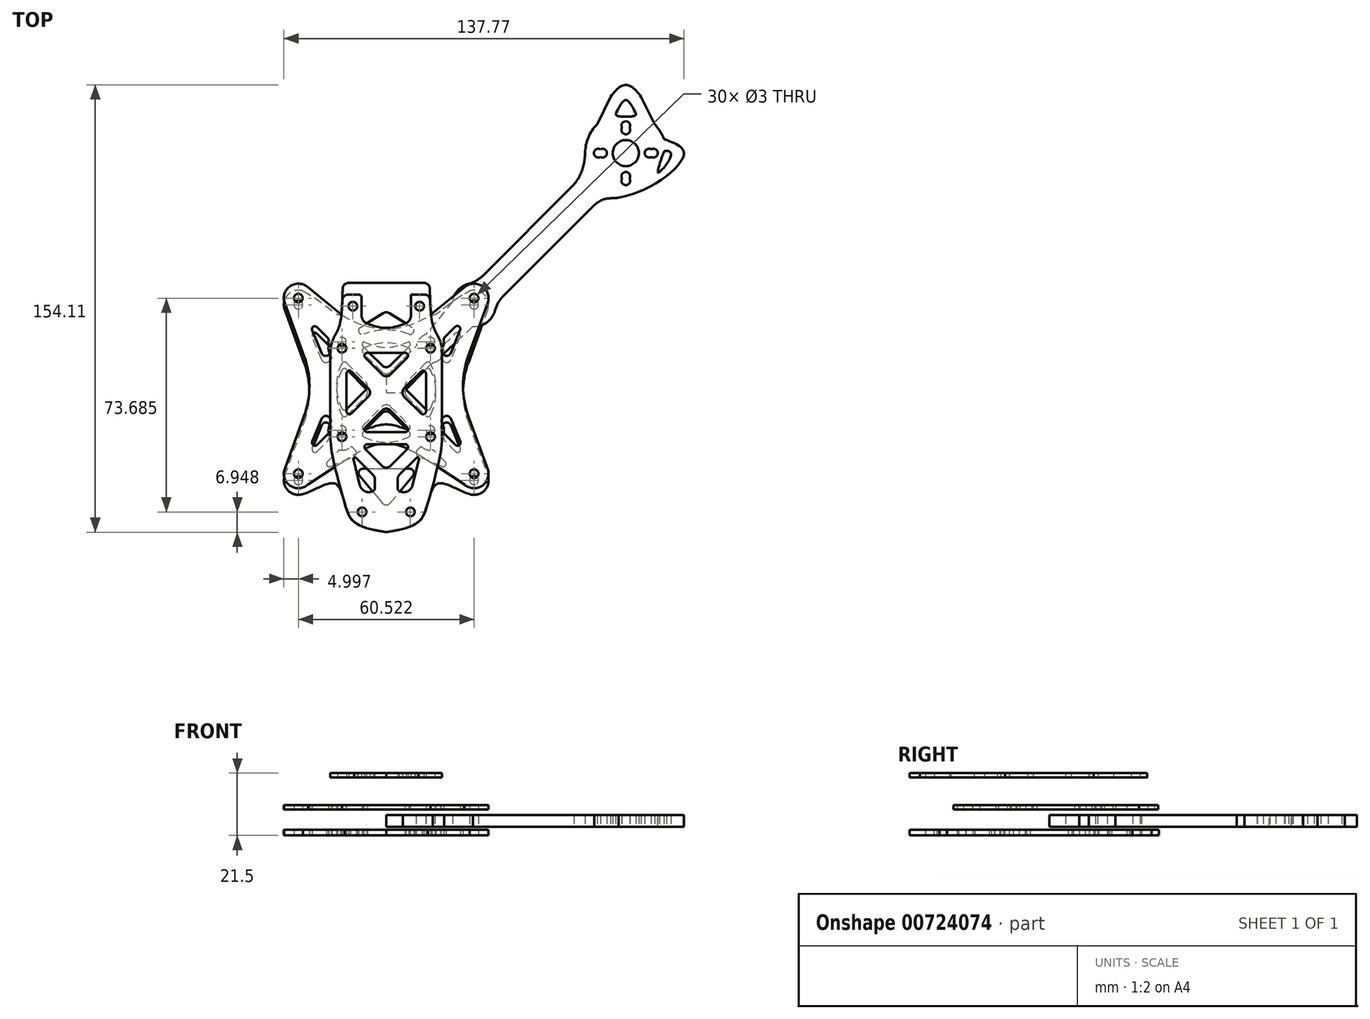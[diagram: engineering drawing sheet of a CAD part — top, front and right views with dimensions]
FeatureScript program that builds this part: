
annotation { "Feature Type Name" : "Feature", "Feature Type Description" : "" }
export const myFeature = defineFeature(function(context is Context, id is Id, definition is map)
    precondition{}
    {
        {
            var Q0;
            Q0=qCreatedBy(makeId("Top.planeOp"),FACE);
            var sketch = newSketch(context, id + "F0", { "sketchPlane" : qUnion([Q0])});
            skLineSegment(sketch, "E0.bottom", {"start": v(-15.25, 15.25) * mm, "end": v(15.25, 15.25) * mm, "construction": true});
            skLineSegment(sketch, "E0.top", {"start": v(-15.25, -15.25) * mm, "end": v(15.25, -15.25) * mm, "construction": true});
            skLineSegment(sketch, "E0.left", {"start": v(-15.25, 15.25) * mm, "end": v(-15.25, -15.25) * mm, "construction": true});
            skLineSegment(sketch, "E0.right", {"start": v(15.25, 15.25) * mm, "end": v(15.25, -15.25) * mm, "construction": true});
            skPoint(sketch, "E0.middle", {"position": v(0, 0) * mm});
            skLineSegment(sketch, "E1.bottom", {"start": v(30.25, 30.25) * mm, "end": v(-30.25, 30.25) * mm, "construction": true});
            skLineSegment(sketch, "E1.top", {"start": v(30.25, -30.25) * mm, "end": v(-30.25, -30.25) * mm, "construction": true});
            skLineSegment(sketch, "E1.left", {"start": v(30.25, 30.25) * mm, "end": v(30.25, -30.25) * mm, "construction": true});
            skLineSegment(sketch, "E1.right", {"start": v(-30.25, 30.25) * mm, "end": v(-30.25, -30.25) * mm, "construction": true});
            skLineSegment(sketch, "E2.bottom", {"start": v(-70.96, 70.96) * mm, "end": v(70.96, 70.96) * mm, "construction": true});
            skLineSegment(sketch, "E2.top", {"start": v(-70.96, -70.96) * mm, "end": v(70.96, -70.96) * mm, "construction": true});
            skLineSegment(sketch, "E2.left", {"start": v(-70.96, 70.96) * mm, "end": v(-70.96, -70.96) * mm, "construction": true});
            skLineSegment(sketch, "E2.right", {"start": v(70.96, 70.96) * mm, "end": v(70.96, -70.96) * mm, "construction": true});
            skCircle(sketch, "E3", {"center": v(70.96, 70.96) * mm, "radius": 8 * mm, "construction": true});
            skCircle(sketch, "E4", {"center": v(70.96, -70.96) * mm, "radius": 8 * mm, "construction": true});
            skCircle(sketch, "E5", {"center": v(-70.96, -70.96) * mm, "radius": 8 * mm, "construction": true});
            skCircle(sketch, "E6", {"center": v(-70.96, 70.96) * mm, "radius": 8 * mm, "construction": true});
            skCircle(sketch, "E7", {"center": v(70.96, 70.96) * mm, "radius": 9.5 * mm, "construction": true});
            skCircle(sketch, "E8", {"center": v(70.96, -70.96) * mm, "radius": 9.5 * mm, "construction": true});
            skCircle(sketch, "E9", {"center": v(-70.96, -70.96) * mm, "radius": 9.5 * mm, "construction": true});
            skCircle(sketch, "E10", {"center": v(-70.96, 70.96) * mm, "radius": 9.5 * mm, "construction": true});
            skCircle(sketch, "E11", {"center": v(70.96, 70.96) * mm, "radius": 14 * mm, "construction": true});
            skCircle(sketch, "E12", {"center": v(-70.96, 70.96) * mm, "radius": 14 * mm, "construction": true});
            skCircle(sketch, "E13", {"center": v(70.96, -70.96) * mm, "radius": 14 * mm, "construction": true});
            skCircle(sketch, "E14", {"center": v(-70.96, -70.96) * mm, "radius": 14 * mm, "construction": true});
            skCircle(sketch, "E15", {"center": v(70.96, 70.96) * mm, "radius": 63.5 * mm, "construction": true});
            skCircle(sketch, "E16", {"center": v(70.96, -70.96) * mm, "radius": 63.5 * mm, "construction": true});
            skCircle(sketch, "E17", {"center": v(-70.96, -70.96) * mm, "radius": 63.5 * mm, "construction": true});
            skCircle(sketch, "E18", {"center": v(-70.96, 70.96) * mm, "radius": 63.5 * mm, "construction": true});
            skLineSegment(sketch, "E19", {"start": v(0, 30.25) * mm, "end": v(0, 37.76) * mm, "construction": true});
            skLineSegment(sketch, "E20", {"start": v(0, 37.76) * mm, "end": v(-15, 37.76) * mm, "construction": true});
            skLineSegment(sketch, "E21", {"start": v(0, 37.76) * mm, "end": v(15, 37.76) * mm, "construction": true});
            skLineSegment(sketch, "E22", {"start": v(0, -30.25) * mm, "end": v(0, -37.76) * mm, "construction": true});
            skLineSegment(sketch, "E23.bottom", {"start": v(-26.17, 26.25) * mm, "end": v(26.21, 26.25) * mm, "construction": true});
            skLineSegment(sketch, "E23.top", {"start": v(-26.21, -26.25) * mm, "end": v(26.17, -26.25) * mm, "construction": true});
            skLineSegment(sketch, "E23.left", {"start": v(-26.17, 26.25) * mm, "end": v(-26.17, -26.13) * mm, "construction": true});
            skLineSegment(sketch, "E23.right", {"start": v(26.21, 26.25) * mm, "end": v(26.21, -26.2) * mm, "construction": true});
            skCircle(sketch, "E24", {"center": v(30.25, 30.25) * mm, "radius": 5 * mm, "construction": true});
            skCircle(sketch, "E25", {"center": v(-30.25, 30.25) * mm, "radius": 5 * mm, "construction": true});
            skCircle(sketch, "E26", {"center": v(30.25, -30.25) * mm, "radius": 5 * mm, "construction": true});
            skCircle(sketch, "E27", {"center": v(-30.25, -30.25) * mm, "radius": 5 * mm, "construction": true});
            skLineSegment(sketch, "E28.bottom", {"start": v(24.5, 24.5) * mm, "end": v(-24.5, 24.5) * mm, "construction": true});
            skLineSegment(sketch, "E28.top", {"start": v(24.5, -24.5) * mm, "end": v(-24.5, -24.5) * mm, "construction": true});
            skLineSegment(sketch, "E28.left", {"start": v(24.5, 24.5) * mm, "end": v(24.5, -24.5) * mm, "construction": true});
            skLineSegment(sketch, "E28.right", {"start": v(-24.5, 24.5) * mm, "end": v(-24.5, -24.5) * mm, "construction": true});
            skLineSegment(sketch, "E29", {"start": v(-26.17, 26.25) * mm, "end": v(-30.25, 30.25) * mm, "construction": true});
            skLineSegment(sketch, "E30", {"start": v(-26.68, 26.75) * mm, "end": v(-33.82, 33.75) * mm, "construction": true});
            skLineSegment(sketch, "E31", {"start": v(-31.8, 31.77) * mm, "end": v(-28.66, 34.99) * mm, "construction": true});
            skLineSegment(sketch, "E32", {"start": v(-31.8, 31.77) * mm, "end": v(-34.96, 28.56) * mm, "construction": true});
            skArc(sketch, "E33", {"start": v(-28.66, 34.99) * mm, "mid": v(-33.82, 33.75) * mm, "end": v(-34.96, 28.56) * mm});
            skLineSegment(sketch, "E34", {"start": v(26.21, 26.25) * mm, "end": v(30.25, 30.25) * mm, "construction": true});
            skLineSegment(sketch, "E35", {"start": v(26.7, 26.73) * mm, "end": v(33.8, 33.77) * mm, "construction": true});
            skLineSegment(sketch, "E36", {"start": v(31.8, 31.78) * mm, "end": v(34.96, 28.58) * mm, "construction": true});
            skLineSegment(sketch, "E37", {"start": v(31.8, 31.78) * mm, "end": v(28.63, 34.98) * mm, "construction": true});
            skArc(sketch, "E38", {"start": v(34.96, 28.58) * mm, "mid": v(33.8, 33.77) * mm, "end": v(28.63, 34.98) * mm});
            skLineSegment(sketch, "E39", {"start": v(26.17, -26.25) * mm, "end": v(30.25, -30.25) * mm, "construction": true});
            skLineSegment(sketch, "E40", {"start": v(26.68, -26.75) * mm, "end": v(33.82, -33.75) * mm, "construction": true});
            skLineSegment(sketch, "E41", {"start": v(31.8, -31.77) * mm, "end": v(34.96, -28.56) * mm, "construction": true});
            skLineSegment(sketch, "E42", {"start": v(31.8, -31.77) * mm, "end": v(28.66, -34.99) * mm, "construction": true});
            skArc(sketch, "E43", {"start": v(28.66, -34.99) * mm, "mid": v(33.82, -33.75) * mm, "end": v(34.96, -28.56) * mm});
            skLineSegment(sketch, "E44", {"start": v(-26.21, -26.25) * mm, "end": v(-30.25, -30.25) * mm, "construction": true});
            skLineSegment(sketch, "E45", {"start": v(-26.7, -26.73) * mm, "end": v(-33.8, -33.77) * mm, "construction": true});
            skLineSegment(sketch, "E46", {"start": v(-31.8, -31.78) * mm, "end": v(-28.63, -34.98) * mm, "construction": true});
            skLineSegment(sketch, "E47", {"start": v(-31.8, -31.78) * mm, "end": v(-34.96, -28.58) * mm, "construction": true});
            skArc(sketch, "E48", {"start": v(-34.96, -28.58) * mm, "mid": v(-33.8, -33.77) * mm, "end": v(-28.63, -34.98) * mm});
            skLineSegment(sketch, "E49", {"start": v(-34.96, -28.58) * mm, "end": v(-28.28, -10.31) * mm});
            skLineSegment(sketch, "E50", {"start": v(-28.28, 10.31) * mm, "end": v(-34.96, 28.56) * mm});
            skLineSegment(sketch, "E51", {"start": v(34.96, 28.58) * mm, "end": v(28.28, 10.31) * mm});
            skLineSegment(sketch, "E52", {"start": v(28.28, -10.31) * mm, "end": v(34.96, -28.56) * mm});
            skPoint(sketch, "E53.visualSharp", {"position": v(24.5, 0) * mm});
            skArc(sketch, "E53.filletArc", {"start": v(28.28, 10.31) * mm, "mid": v(26.45, 0) * mm, "end": v(28.28, -10.31) * mm});
            skPoint(sketch, "E54.visualSharp", {"position": v(-24.5, 0) * mm});
            skArc(sketch, "E54.filletArc", {"start": v(-28.28, -10.31) * mm, "mid": v(-26.45, 0) * mm, "end": v(-28.28, 10.31) * mm});
            skFitSpline(sketch, "E55", {"points": [v(-28.66, 34.99) * mm, v(-15, 37.76) * mm], "startDerivative": vector(40.9, -21.49) * mm, "endDerivative": vector(0.75, 54.16) * mm});
            skFitSpline(sketch, "E56", {"points": [v(15, 37.76) * mm, v(28.63, 34.98) * mm], "startDerivative": vector(0.75, -54.16) * mm, "endDerivative": vector(40.9, 21.46) * mm});
            skLineSegment(sketch, "E57", {"start": v(-15.25, 19.7) * mm, "end": v(15.25, 19.7) * mm, "construction": true});
            skPoint(sketch, "E58.endSnap0", {"position": v(0, -15.25) * mm});
            skLineSegment(sketch, "E59", {"start": v(-15.25, -19.7) * mm, "end": v(15.25, -19.7) * mm, "construction": true});
            skLineSegment(sketch, "E60", {"start": v(-14.33, -37.76) * mm, "end": v(14.33, -37.76) * mm, "construction": true});
            skLineSegment(sketch, "E61", {"start": v(-13.03, 37.76) * mm, "end": v(13.03, 37.76) * mm});
            skCircle(sketch, "E62", {"center": v(-30.25, 30.25) * mm, "radius": 1.5 * mm});
            skCircle(sketch, "E63", {"center": v(30.25, 30.25) * mm, "radius": 1.5 * mm});
            skCircle(sketch, "E64", {"center": v(15.25, 15.25) * mm, "radius": 1.5 * mm});
            skCircle(sketch, "E65", {"center": v(-15.25, 15.25) * mm, "radius": 1.5 * mm});
            skCircle(sketch, "E66", {"center": v(-15.25, -15.25) * mm, "radius": 1.5 * mm});
            skCircle(sketch, "E67", {"center": v(15.25, -15.25) * mm, "radius": 1.5 * mm});
            skCircle(sketch, "E68", {"center": v(30.25, -30.25) * mm, "radius": 1.5 * mm});
            skCircle(sketch, "E69", {"center": v(-30.25, -30.25) * mm, "radius": 1.5 * mm});
            skLineSegment(sketch, "E70", {"start": v(15, 37.76) * mm, "end": v(11.5, 37.76) * mm, "construction": true});
            skLineSegment(sketch, "E71", {"start": v(-15, 37.76) * mm, "end": v(-11.5, 37.76) * mm, "construction": true});
            skLineSegment(sketch, "E72", {"start": v(11.5, 37.76) * mm, "end": v(11.5, 29.76) * mm, "construction": true});
            skLineSegment(sketch, "E73", {"start": v(-11.5, 37.76) * mm, "end": v(-11.5, 29.76) * mm, "construction": true});
            skCircle(sketch, "E74", {"center": v(-11.5, 29.76) * mm, "radius": 1.5 * mm});
            skCircle(sketch, "E75", {"center": v(11.5, 29.76) * mm, "radius": 1.5 * mm});
            skLineSegment(sketch, "E76", {"start": v(0, 37.76) * mm, "end": v(0, 15.25) * mm, "construction": true});
            skLineSegment(sketch, "E77", {"start": v(0, -44.58) * mm, "end": v(-11, -44.58) * mm, "construction": true});
            skLineSegment(sketch, "E78", {"start": v(0, -44.58) * mm, "end": v(11, -44.58) * mm, "construction": true});
            skPoint(sketch, "E79.visualSharp", {"position": v(-14.33, -37.76) * mm});
            skPoint(sketch, "E80.visualSharp", {"position": v(14.33, -37.76) * mm});
            skCircle(sketch, "E81", {"center": v(0, 0) * mm, "radius": 17.11 * mm, "construction": true});
            skLineSegment(sketch, "E82", {"start": v(0, 0) * mm, "end": v(14.1, 14.1) * mm, "construction": true});
            skLineSegment(sketch, "E83", {"start": v(0, 0) * mm, "end": v(-15.25, 15.25) * mm, "construction": true});
            skLineSegment(sketch, "E84", {"start": v(0, 0) * mm, "end": v(-15.32, -15.32) * mm, "construction": true});
            skLineSegment(sketch, "E85", {"start": v(0, 0) * mm, "end": v(15.25, -15.25) * mm, "construction": true});
            skLineSegment(sketch, "E86", {"start": v(-10.7, 10.7) * mm, "end": v(-7.86, 13.52) * mm, "construction": true});
            skLineSegment(sketch, "E87", {"start": v(-10.7, 10.7) * mm, "end": v(-13.52, 7.86) * mm, "construction": true});
            skLineSegment(sketch, "E88", {"start": v(9.03, 9.03) * mm, "end": v(11.86, 6.2) * mm, "construction": true});
            skLineSegment(sketch, "E89", {"start": v(9.03, 9.03) * mm, "end": v(6.2, 11.86) * mm, "construction": true});
            skLineSegment(sketch, "E90", {"start": v(9.8, -9.8) * mm, "end": v(12.64, -6.98) * mm, "construction": true});
            skLineSegment(sketch, "E91", {"start": v(9.8, -9.8) * mm, "end": v(6.98, -12.64) * mm, "construction": true});
            skLineSegment(sketch, "E92", {"start": v(-9.52, -9.52) * mm, "end": v(-6.7, -12.35) * mm, "construction": true});
            skLineSegment(sketch, "E93", {"start": v(-9.52, -9.52) * mm, "end": v(-12.35, -6.7) * mm, "construction": true});
            skLineSegment(sketch, "E94.bottom", {"start": v(6.35, 6.35) * mm, "end": v(-6.35, 6.35) * mm, "construction": true});
            skLineSegment(sketch, "E94.top", {"start": v(6.35, -6.35) * mm, "end": v(-6.35, -6.35) * mm, "construction": true});
            skLineSegment(sketch, "E94.left", {"start": v(6.35, 6.35) * mm, "end": v(6.35, -6.35) * mm, "construction": true});
            skLineSegment(sketch, "E94.right", {"start": v(-6.35, 6.35) * mm, "end": v(-6.35, -6.35) * mm, "construction": true});
            skLineSegment(sketch, "E95", {"start": v(6.2, 11.86) * mm, "end": v(8.94, 14.6) * mm, "construction": true});
            skLineSegment(sketch, "E96", {"start": v(11.86, 6.2) * mm, "end": v(14.6, 8.94) * mm, "construction": true});
            skLineSegment(sketch, "E97", {"start": v(8, 13.66) * mm, "end": v(1.41, 7.07) * mm});
            skLineSegment(sketch, "E98", {"start": v(-1.41, 7.07) * mm, "end": v(-8, 13.66) * mm});
            skLineSegment(sketch, "E99", {"start": v(-13.52, 7.86) * mm, "end": v(-14.6, 8.94) * mm, "construction": true});
            skLineSegment(sketch, "E100", {"start": v(-6.7, -12.35) * mm, "end": v(-8.94, -14.6) * mm, "construction": true});
            skLineSegment(sketch, "E101", {"start": v(-8, -13.66) * mm, "end": v(-1.41, -7.07) * mm});
            skLineSegment(sketch, "E102", {"start": v(1.41, -7.07) * mm, "end": v(8, -13.66) * mm});
            skLineSegment(sketch, "E103", {"start": v(13.66, 8) * mm, "end": v(7.07, 1.41) * mm});
            skLineSegment(sketch, "E104", {"start": v(7.07, -1.41) * mm, "end": v(13.66, -8) * mm});
            skPoint(sketch, "E105", {"position": v(-7.77, 15.25) * mm});
            skPoint(sketch, "E106", {"position": v(7.77, 15.25) * mm});
            skPoint(sketch, "E107", {"position": v(15.25, 7.77) * mm});
            skPoint(sketch, "E108", {"position": v(15.25, -7.77) * mm});
            skPoint(sketch, "E109", {"position": v(7.77, -15.25) * mm});
            skPoint(sketch, "E110", {"position": v(-7.77, -15.25) * mm});
            skPoint(sketch, "E111", {"position": v(-15.25, -7.77) * mm});
            skPoint(sketch, "E112", {"position": v(-15.25, 7.77) * mm});
            skLineSegment(sketch, "E113", {"start": v(-7.79, 15.24) * mm, "end": v(-7.77, 15.25) * mm});
            skLineSegment(sketch, "E114", {"start": v(7.79, 15.24) * mm, "end": v(7.77, 15.25) * mm});
            skLineSegment(sketch, "E115", {"start": v(15.24, 7.79) * mm, "end": v(15.25, 7.77) * mm});
            skLineSegment(sketch, "E116", {"start": v(15.24, -7.79) * mm, "end": v(15.25, -7.77) * mm});
            skLineSegment(sketch, "E117", {"start": v(7.79, -15.24) * mm, "end": v(7.77, -15.25) * mm});
            skLineSegment(sketch, "E118", {"start": v(-7.77, -15.25) * mm, "end": v(-7.79, -15.24) * mm});
            skLineSegment(sketch, "E119", {"start": v(-15.24, -7.79) * mm, "end": v(-15.25, -7.77) * mm});
            skLineSegment(sketch, "E120", {"start": v(-15.24, 7.79) * mm, "end": v(-15.25, 7.77) * mm});
            skPoint(sketch, "E121", {"position": v(0, 17.11) * mm});
            skPoint(sketch, "E122", {"position": v(17.11, 0) * mm});
            skPoint(sketch, "E123", {"position": v(-17.11, 0) * mm});
            skPoint(sketch, "E124", {"position": v(0, -17.11) * mm});
            skArc(sketch, "E125", {"start": v(7.77, 15.25) * mm, "mid": v(0, 17.11) * mm, "end": v(-7.77, 15.25) * mm});
            skArc(sketch, "E126", {"start": v(15.25, -7.77) * mm, "mid": v(17.11, 0) * mm, "end": v(15.25, 7.77) * mm});
            skArc(sketch, "E127", {"start": v(-7.77, -15.25) * mm, "mid": v(0, -17.11) * mm, "end": v(7.77, -15.25) * mm});
            skArc(sketch, "E128", {"start": v(-15.25, 7.77) * mm, "mid": v(-17.11, 0) * mm, "end": v(-15.25, -7.77) * mm});
            skPoint(sketch, "E129.visualSharp", {"position": v(-5.66, 0) * mm});
            skPoint(sketch, "E130.visualSharp", {"position": v(-14.6, 8.94) * mm});
            skArc(sketch, "E130.filletArc", {"start": v(-13.66, 8) * mm, "mid": v(-14.5, 8.29) * mm, "end": v(-15.24, 7.79) * mm});
            skPoint(sketch, "E131.visualSharp", {"position": v(-14.6, -8.94) * mm});
            skArc(sketch, "E131.filletArc", {"start": v(-15.24, -7.79) * mm, "mid": v(-14.5, -8.29) * mm, "end": v(-13.66, -8) * mm});
            skPoint(sketch, "E132.visualSharp", {"position": v(-8.94, 14.6) * mm});
            skArc(sketch, "E132.filletArc", {"start": v(-7.79, 15.24) * mm, "mid": v(-8.29, 14.5) * mm, "end": v(-8, 13.66) * mm});
            skPoint(sketch, "E133.visualSharp", {"position": v(8.94, 14.6) * mm});
            skArc(sketch, "E133.filletArc", {"start": v(8, 13.66) * mm, "mid": v(8.29, 14.5) * mm, "end": v(7.79, 15.24) * mm});
            skPoint(sketch, "E134.visualSharp", {"position": v(14.6, -8.94) * mm});
            skArc(sketch, "E134.filletArc", {"start": v(13.66, -8) * mm, "mid": v(14.5, -8.29) * mm, "end": v(15.24, -7.79) * mm});
            skPoint(sketch, "E135.visualSharp", {"position": v(14.6, 8.94) * mm});
            skArc(sketch, "E135.filletArc", {"start": v(15.24, 7.79) * mm, "mid": v(14.5, 8.29) * mm, "end": v(13.66, 8) * mm});
            skPoint(sketch, "E136.visualSharp", {"position": v(8.94, -14.6) * mm});
            skArc(sketch, "E136.filletArc", {"start": v(7.79, -15.24) * mm, "mid": v(8.29, -14.5) * mm, "end": v(8, -13.66) * mm});
            skPoint(sketch, "E137.visualSharp", {"position": v(-8.94, -14.6) * mm});
            skArc(sketch, "E137.filletArc", {"start": v(-8, -13.66) * mm, "mid": v(-8.29, -14.5) * mm, "end": v(-7.79, -15.24) * mm});
            skLineSegment(sketch, "E138", {"start": v(-13.66, 8) * mm, "end": v(-7.07, 1.41) * mm});
            skLineSegment(sketch, "E139", {"start": v(-13.66, -8) * mm, "end": v(-7.07, -1.41) * mm});
            skArc(sketch, "E140.filletArc", {"start": v(-7.07, -1.41) * mm, "mid": v(-6.49, 0) * mm, "end": v(-7.07, 1.41) * mm});
            skPoint(sketch, "E141.visualSharp", {"position": v(0, -5.66) * mm});
            skArc(sketch, "E141.filletArc", {"start": v(1.41, -7.07) * mm, "mid": v(0, -6.49) * mm, "end": v(-1.41, -7.07) * mm});
            skPoint(sketch, "E142.visualSharp", {"position": v(5.66, 0) * mm});
            skArc(sketch, "E142.filletArc", {"start": v(7.07, 1.41) * mm, "mid": v(6.49, 0) * mm, "end": v(7.07, -1.41) * mm});
            skPoint(sketch, "E143.visualSharp", {"position": v(0, 5.66) * mm});
            skArc(sketch, "E143.filletArc", {"start": v(-1.41, 7.07) * mm, "mid": v(0, 6.49) * mm, "end": v(1.41, 7.07) * mm});
            skLineSegment(sketch, "E144", {"start": v(-12.9, 12.9) * mm, "end": v(-11.14, 14.67) * mm, "construction": true});
            skLineSegment(sketch, "E145", {"start": v(-12.9, 12.9) * mm, "end": v(-14.67, 11.14) * mm, "construction": true});
            skLineSegment(sketch, "E146", {"start": v(-14.67, 11.14) * mm, "end": v(-27.4, 23.87) * mm, "construction": true});
            skPoint(sketch, "E147", {"position": v(-17.57, 14.03) * mm});
            skCircle(sketch, "E148", {"center": v(-15.25, 15.25) * mm, "radius": 4.62 * mm, "construction": true});
            skLineSegment(sketch, "E149", {"start": v(-27.4, 23.87) * mm, "end": v(-21.1, 8.64) * mm, "construction": true});
            skLineSegment(sketch, "E150", {"start": v(-15.25, 15.25) * mm, "end": v(-21.32, 9.18) * mm, "construction": true});
            skLineSegment(sketch, "E151", {"start": v(-18.86, 11.64) * mm, "end": v(-19.74, 10.76) * mm});
            skLineSegment(sketch, "E152", {"start": v(-22.18, 11.25) * mm, "end": v(-25.48, 19.23) * mm});
            skLineSegment(sketch, "E153", {"start": v(-23.85, 20.32) * mm, "end": v(-20.04, 16.5) * mm});
            skLineSegment(sketch, "E154", {"start": v(-19.83, 15.85) * mm, "end": v(-19.85, 15.74) * mm});
            skLineSegment(sketch, "E155", {"start": v(-18.84, 12.33) * mm, "end": v(-18.85, 12.35) * mm});
            skPoint(sketch, "E156", {"position": v(-19.67, 13.9) * mm});
            skArc(sketch, "E157", {"start": v(-19.85, 15.74) * mm, "mid": v(-19.69, 13.95) * mm, "end": v(-18.85, 12.35) * mm});
            skPoint(sketch, "E158.visualSharp", {"position": v(-27.4, 23.87) * mm});
            skArc(sketch, "E158.filletArc", {"start": v(-23.85, 20.32) * mm, "mid": v(-25.11, 20.44) * mm, "end": v(-25.48, 19.23) * mm});
            skPoint(sketch, "E159.visualSharp", {"position": v(-21.32, 9.18) * mm});
            skArc(sketch, "E159.filletArc", {"start": v(-22.18, 11.25) * mm, "mid": v(-21.1, 10.35) * mm, "end": v(-19.74, 10.76) * mm});
            skPoint(sketch, "E160.visualSharp", {"position": v(-18.52, 11.98) * mm});
            skArc(sketch, "E160.filletArc", {"start": v(-18.86, 11.64) * mm, "mid": v(-18.7, 11.98) * mm, "end": v(-18.84, 12.33) * mm});
            skPoint(sketch, "E161.visualSharp", {"position": v(-19.77, 16.23) * mm});
            skArc(sketch, "E161.filletArc", {"start": v(-19.83, 15.85) * mm, "mid": v(-19.86, 16.2) * mm, "end": v(-20.04, 16.5) * mm});
            skCircle(sketch, "E162", {"center": v(15.23, 15.26) * mm, "radius": 4.62 * mm, "construction": true});
            skLineSegment(sketch, "E163", {"start": v(15.23, 15.26) * mm, "end": v(12.9, 12.9) * mm, "construction": true});
            skLineSegment(sketch, "E164", {"start": v(12.9, 12.9) * mm, "end": v(14.68, 11.15) * mm, "construction": true});
            skLineSegment(sketch, "E165", {"start": v(12.9, 12.9) * mm, "end": v(11.12, 14.66) * mm, "construction": true});
            skLineSegment(sketch, "E166", {"start": v(11.12, 14.66) * mm, "end": v(23.85, 27.39) * mm, "construction": true});
            skLineSegment(sketch, "E167", {"start": v(14.68, 11.15) * mm, "end": v(27.32, 23.97) * mm, "construction": true});
            skLineSegment(sketch, "E168", {"start": v(15.25, 15.25) * mm, "end": v(21.37, 9.22) * mm, "construction": true});
            skLineSegment(sketch, "E169", {"start": v(21.37, 9.22) * mm, "end": v(27.32, 23.97) * mm, "construction": true});
            skLineSegment(sketch, "E170", {"start": v(19.8, 15.9) * mm, "end": v(19.82, 15.79) * mm});
            skLineSegment(sketch, "E171", {"start": v(18.84, 12.37) * mm, "end": v(18.86, 12.4) * mm});
            skLineSegment(sketch, "E172", {"start": v(20.01, 16.55) * mm, "end": v(23.8, 20.4) * mm});
            skLineSegment(sketch, "E173", {"start": v(25.45, 19.33) * mm, "end": v(22.2, 11.3) * mm});
            skLineSegment(sketch, "E174", {"start": v(19.77, 10.8) * mm, "end": v(18.86, 11.69) * mm});
            skPoint(sketch, "E175", {"position": v(19.65, 13.92) * mm});
            skArc(sketch, "E176", {"start": v(18.86, 12.4) * mm, "mid": v(19.68, 14) * mm, "end": v(19.82, 15.79) * mm});
            skPoint(sketch, "E177.visualSharp", {"position": v(18.53, 12.02) * mm});
            skArc(sketch, "E177.filletArc", {"start": v(18.84, 12.37) * mm, "mid": v(18.72, 12.03) * mm, "end": v(18.86, 11.69) * mm});
            skPoint(sketch, "E178.visualSharp", {"position": v(19.74, 16.28) * mm});
            skArc(sketch, "E178.filletArc", {"start": v(20.01, 16.55) * mm, "mid": v(19.83, 16.25) * mm, "end": v(19.8, 15.9) * mm});
            skPoint(sketch, "E179.visualSharp", {"position": v(27.32, 23.97) * mm});
            skArc(sketch, "E179.filletArc", {"start": v(25.45, 19.33) * mm, "mid": v(25.07, 20.54) * mm, "end": v(23.8, 20.4) * mm});
            skPoint(sketch, "E180.visualSharp", {"position": v(21.37, 9.22) * mm});
            skArc(sketch, "E180.filletArc", {"start": v(19.77, 10.8) * mm, "mid": v(21.12, 10.4) * mm, "end": v(22.2, 11.3) * mm});
            skCircle(sketch, "E181", {"center": v(-15.25, -15.25) * mm, "radius": 4.62 * mm, "construction": true});
            skCircle(sketch, "E182", {"center": v(15.25, -15.25) * mm, "radius": 4.62 * mm, "construction": true});
            skLineSegment(sketch, "E183", {"start": v(-15.25, -15.25) * mm, "end": v(-12.9, -12.9) * mm, "construction": true});
            skLineSegment(sketch, "E184", {"start": v(-12.9, -12.9) * mm, "end": v(-11.14, -14.67) * mm, "construction": true});
            skLineSegment(sketch, "E185", {"start": v(-12.9, -12.9) * mm, "end": v(-14.67, -11.14) * mm, "construction": true});
            skLineSegment(sketch, "E186", {"start": v(-11.14, -14.67) * mm, "end": v(-23.87, -27.4) * mm, "construction": true});
            skLineSegment(sketch, "E187", {"start": v(-14.67, -11.14) * mm, "end": v(-27.4, -23.87) * mm, "construction": true});
            skLineSegment(sketch, "E188", {"start": v(-15.25, -15.25) * mm, "end": v(-9.18, -21.32) * mm, "construction": true});
            skLineSegment(sketch, "E189", {"start": v(-15.25, -15.25) * mm, "end": v(-21.32, -9.18) * mm, "construction": true});
            skLineSegment(sketch, "E190", {"start": v(-25.48, -19.23) * mm, "end": v(-22.18, -11.25) * mm});
            skLineSegment(sketch, "E191", {"start": v(-19.74, -10.76) * mm, "end": v(-18.86, -11.64) * mm});
            skLineSegment(sketch, "E192", {"start": v(-23.85, -20.32) * mm, "end": v(-20.04, -16.5) * mm});
            skLineSegment(sketch, "E193", {"start": v(-18.84, -12.33) * mm, "end": v(-18.85, -12.35) * mm});
            skLineSegment(sketch, "E194", {"start": v(-19.83, -15.85) * mm, "end": v(-19.85, -15.74) * mm});
            skPoint(sketch, "E195", {"position": v(-19.69, -13.94) * mm});
            skArc(sketch, "E196", {"start": v(-18.85, -12.35) * mm, "mid": v(-19.69, -13.95) * mm, "end": v(-19.85, -15.74) * mm});
            skPoint(sketch, "E197.visualSharp", {"position": v(-18.52, -11.98) * mm});
            skArc(sketch, "E197.filletArc", {"start": v(-18.84, -12.33) * mm, "mid": v(-18.7, -11.98) * mm, "end": v(-18.86, -11.64) * mm});
            skPoint(sketch, "E198.visualSharp", {"position": v(-19.77, -16.23) * mm});
            skArc(sketch, "E198.filletArc", {"start": v(-20.04, -16.5) * mm, "mid": v(-19.86, -16.2) * mm, "end": v(-19.83, -15.85) * mm});
            skPoint(sketch, "E199.visualSharp", {"position": v(-27.4, -23.87) * mm});
            skArc(sketch, "E199.filletArc", {"start": v(-25.48, -19.23) * mm, "mid": v(-25.11, -20.44) * mm, "end": v(-23.85, -20.32) * mm});
            skPoint(sketch, "E200.visualSharp", {"position": v(-21.32, -9.18) * mm});
            skArc(sketch, "E200.filletArc", {"start": v(-19.74, -10.76) * mm, "mid": v(-21.1, -10.35) * mm, "end": v(-22.18, -11.25) * mm});
            skLineSegment(sketch, "E201", {"start": v(15.25, -15.25) * mm, "end": v(12.9, -12.9) * mm, "construction": true});
            skLineSegment(sketch, "E202", {"start": v(12.9, -12.9) * mm, "end": v(14.67, -11.14) * mm, "construction": true});
            skLineSegment(sketch, "E203", {"start": v(12.9, -12.9) * mm, "end": v(11.14, -14.67) * mm, "construction": true});
            skLineSegment(sketch, "E204", {"start": v(14.67, -11.14) * mm, "end": v(27.4, -23.87) * mm, "construction": true});
            skLineSegment(sketch, "E205", {"start": v(15.25, -15.25) * mm, "end": v(21.32, -9.18) * mm, "construction": true});
            skLineSegment(sketch, "E206", {"start": v(22.18, -11.25) * mm, "end": v(25.48, -19.23) * mm});
            skLineSegment(sketch, "E207", {"start": v(23.85, -20.32) * mm, "end": v(20.04, -16.5) * mm});
            skLineSegment(sketch, "E208", {"start": v(19.74, -10.76) * mm, "end": v(18.86, -11.64) * mm});
            skLineSegment(sketch, "E209", {"start": v(18.84, -12.33) * mm, "end": v(18.85, -12.35) * mm});
            skLineSegment(sketch, "E210", {"start": v(19.83, -15.85) * mm, "end": v(19.85, -15.74) * mm});
            skPoint(sketch, "E211", {"position": v(19.64, -13.8) * mm});
            skArc(sketch, "E212", {"start": v(19.85, -15.74) * mm, "mid": v(19.69, -13.95) * mm, "end": v(18.85, -12.35) * mm});
            skPoint(sketch, "E213.visualSharp", {"position": v(21.32, -9.18) * mm});
            skArc(sketch, "E213.filletArc", {"start": v(22.18, -11.25) * mm, "mid": v(21.1, -10.35) * mm, "end": v(19.74, -10.76) * mm});
            skPoint(sketch, "E214.visualSharp", {"position": v(19.77, -16.23) * mm});
            skArc(sketch, "E214.filletArc", {"start": v(19.83, -15.85) * mm, "mid": v(19.86, -16.2) * mm, "end": v(20.04, -16.5) * mm});
            skPoint(sketch, "E215.visualSharp", {"position": v(18.52, -11.98) * mm});
            skArc(sketch, "E215.filletArc", {"start": v(18.86, -11.64) * mm, "mid": v(18.7, -11.98) * mm, "end": v(18.84, -12.33) * mm});
            skPoint(sketch, "E216.visualSharp", {"position": v(27.4, -23.87) * mm});
            skArc(sketch, "E216.filletArc", {"start": v(23.85, -20.32) * mm, "mid": v(25.11, -20.44) * mm, "end": v(25.48, -19.23) * mm});
            skPoint(sketch, "E217", {"position": v(0, -48.1) * mm});
            skLineSegment(sketch, "E218", {"start": v(0, -31.42) * mm, "end": v(17.54, -31.42) * mm, "construction": true});
            skLineSegment(sketch, "E219", {"start": v(0, -31.42) * mm, "end": v(-17.54, -31.42) * mm, "construction": true});
            skFitSpline(sketch, "E220", {"points": [v(28.66, -34.99) * mm, v(17.54, -31.42) * mm, v(14.33, -37.76) * mm], "startDerivative": vector(-22.15, 6.9) * mm, "endDerivative": vector(-5.52, -13.66) * mm});
            skFitSpline(sketch, "E221", {"points": [v(14.33, -37.76) * mm, v(11, -44.58) * mm, v(0, -48.1) * mm], "startDerivative": vector(-4.65, -17.21) * mm, "endDerivative": vector(-23.36, -3.95) * mm});
            skFitSpline(sketch, "E222", {"points": [v(-28.63, -34.98) * mm, v(-17.54, -31.42) * mm, v(-14.33, -37.76) * mm], "startDerivative": vector(22.11, 6.89) * mm, "endDerivative": vector(5.52, -13.65) * mm});
            skFitSpline(sketch, "E223", {"points": [v(-14.33, -37.76) * mm, v(-11, -44.58) * mm, v(0, -48.1) * mm], "startDerivative": vector(4.65, -17.21) * mm, "endDerivative": vector(23.36, -3.95) * mm});
            skLineSegment(sketch, "E224", {"start": v(-19.23, -25.48) * mm, "end": v(-11.25, -22.18) * mm});
            skLineSegment(sketch, "E225", {"start": v(-10.76, -19.74) * mm, "end": v(-11.64, -18.86) * mm});
            skLineSegment(sketch, "E226", {"start": v(-12.33, -18.84) * mm, "end": v(-12.35, -18.85) * mm});
            skLineSegment(sketch, "E227", {"start": v(-20.32, -23.85) * mm, "end": v(-16.5, -20.04) * mm});
            skLineSegment(sketch, "E228", {"start": v(-15.85, -19.83) * mm, "end": v(-15.74, -19.85) * mm});
            skPoint(sketch, "E229.visualSharp", {"position": v(-9.18, -21.32) * mm});
            skArc(sketch, "E229.filletArc", {"start": v(-11.25, -22.18) * mm, "mid": v(-10.35, -21.1) * mm, "end": v(-10.76, -19.74) * mm});
            skPoint(sketch, "E230.visualSharp", {"position": v(-11.98, -18.52) * mm});
            skArc(sketch, "E230.filletArc", {"start": v(-11.64, -18.86) * mm, "mid": v(-11.98, -18.7) * mm, "end": v(-12.33, -18.84) * mm});
            skPoint(sketch, "E231.visualSharp", {"position": v(-16.23, -19.77) * mm});
            skArc(sketch, "E231.filletArc", {"start": v(-15.85, -19.83) * mm, "mid": v(-16.2, -19.86) * mm, "end": v(-16.5, -20.04) * mm});
            skPoint(sketch, "E232.visualSharp", {"position": v(-23.87, -27.4) * mm});
            skArc(sketch, "E232.filletArc", {"start": v(-20.32, -23.85) * mm, "mid": v(-20.44, -25.11) * mm, "end": v(-19.23, -25.48) * mm});
            skLineSegment(sketch, "E233", {"start": v(15.25, -15.25) * mm, "end": v(9.18, -21.32) * mm, "construction": true});
            skLineSegment(sketch, "E234", {"start": v(11.14, -14.67) * mm, "end": v(23.87, -27.4) * mm, "construction": true});
            skLineSegment(sketch, "E235", {"start": v(19.23, -25.48) * mm, "end": v(11.25, -22.18) * mm});
            skLineSegment(sketch, "E236", {"start": v(10.76, -19.74) * mm, "end": v(11.64, -18.86) * mm});
            skLineSegment(sketch, "E237", {"start": v(12.33, -18.84) * mm, "end": v(12.35, -18.85) * mm});
            skLineSegment(sketch, "E238", {"start": v(20.32, -23.85) * mm, "end": v(16.5, -20.04) * mm});
            skLineSegment(sketch, "E239", {"start": v(15.85, -19.83) * mm, "end": v(15.74, -19.85) * mm});
            skPoint(sketch, "E240", {"position": v(13.76, -19.63) * mm});
            skArc(sketch, "E241", {"start": v(12.35, -18.85) * mm, "mid": v(13.95, -19.69) * mm, "end": v(15.74, -19.85) * mm});
            skPoint(sketch, "E242.visualSharp", {"position": v(9.18, -21.32) * mm});
            skArc(sketch, "E242.filletArc", {"start": v(10.76, -19.74) * mm, "mid": v(10.35, -21.1) * mm, "end": v(11.25, -22.18) * mm});
            skPoint(sketch, "E243.visualSharp", {"position": v(11.98, -18.52) * mm});
            skArc(sketch, "E243.filletArc", {"start": v(12.33, -18.84) * mm, "mid": v(11.98, -18.7) * mm, "end": v(11.64, -18.86) * mm});
            skPoint(sketch, "E244.visualSharp", {"position": v(23.87, -27.4) * mm});
            skArc(sketch, "E244.filletArc", {"start": v(19.23, -25.48) * mm, "mid": v(20.44, -25.11) * mm, "end": v(20.32, -23.85) * mm});
            skPoint(sketch, "E245.visualSharp", {"position": v(16.23, -19.77) * mm});
            skArc(sketch, "E245.filletArc", {"start": v(16.5, -20.04) * mm, "mid": v(16.2, -19.86) * mm, "end": v(15.85, -19.83) * mm});
            skPoint(sketch, "E246", {"position": v(-14.29, -19.77) * mm});
            skArc(sketch, "E247", {"start": v(-15.74, -19.85) * mm, "mid": v(-13.95, -19.69) * mm, "end": v(-12.35, -18.85) * mm});
            skArc(sketch, "E248.filletArc", {"start": v(-13.03, 37.76) * mm, "mid": v(-14.43, 37.18) * mm, "end": v(-15.03, 35.79) * mm});
            skArc(sketch, "E249.filletArc", {"start": v(15.03, 35.79) * mm, "mid": v(14.43, 37.18) * mm, "end": v(13.03, 37.76) * mm});
            skLineSegment(sketch, "E250", {"start": v(-13.27, -41.16) * mm, "end": v(-8.27, -41.16) * mm, "construction": true});
            skLineSegment(sketch, "E251", {"start": v(-8.27, -41.16) * mm, "end": v(-8.27, -46.16) * mm, "construction": true});
            skLineSegment(sketch, "E252", {"start": v(13.27, -41.16) * mm, "end": v(8.27, -41.16) * mm, "construction": true});
            skLineSegment(sketch, "E253", {"start": v(8.27, -41.16) * mm, "end": v(8.27, -46.16) * mm, "construction": true});
            skCircle(sketch, "E254", {"center": v(8.27, -41.16) * mm, "radius": 1.5 * mm});
            skCircle(sketch, "E255", {"center": v(-8.27, -41.16) * mm, "radius": 1.5 * mm});
            skLineSegment(sketch, "E256", {"start": v(-8.94, 14.6) * mm, "end": v(-8.94, 19.63) * mm, "construction": true});
            skLineSegment(sketch, "E257", {"start": v(8.94, 14.6) * mm, "end": v(8.94, 19.63) * mm, "construction": true});
            skPoint(sketch, "E258", {"position": v(0, 21.57) * mm});
            skLineSegment(sketch, "E259", {"start": v(-7.77, 15.25) * mm, "end": v(-7.77, 20.12) * mm, "construction": true});
            skLineSegment(sketch, "E260", {"start": v(7.79, 15.24) * mm, "end": v(7.79, 20.11) * mm, "construction": true});
            skLineSegment(sketch, "E261", {"start": v(-8.94, 19.63) * mm, "end": v(-8.94, 22.43) * mm, "construction": true});
            skLineSegment(sketch, "E262", {"start": v(8.94, 19.63) * mm, "end": v(8.94, 22.43) * mm, "construction": true});
            skLineSegment(sketch, "E263", {"start": v(-8.94, 22.43) * mm, "end": v(-1.06, 27.36) * mm});
            skLineSegment(sketch, "E264", {"start": v(1.06, 27.36) * mm, "end": v(8.94, 22.43) * mm});
            skArc(sketch, "E265", {"start": v(-8.94, 22.43) * mm, "mid": v(-9.4, 20.74) * mm, "end": v(-7.77, 20.12) * mm});
            skArc(sketch, "E266", {"start": v(7.79, 20.11) * mm, "mid": v(9.41, 20.75) * mm, "end": v(8.94, 22.43) * mm});
            skPoint(sketch, "E267.visualSharp", {"position": v(0, 28.02) * mm});
            skArc(sketch, "E267.filletArc", {"start": v(1.06, 27.36) * mm, "mid": v(0, 27.66) * mm, "end": v(-1.06, 27.36) * mm});
            skArc(sketch, "E268", {"start": v(7.79, 20.11) * mm, "mid": v(0, 21.57) * mm, "end": v(-7.77, 20.12) * mm});
            skLineSegment(sketch, "E269", {"start": v(-8.94, -14.6) * mm, "end": v(-8.94, -19.63) * mm, "construction": true});
            skLineSegment(sketch, "E270", {"start": v(-7.77, -15.25) * mm, "end": v(-7.77, -20.12) * mm, "construction": true});
            skLineSegment(sketch, "E271", {"start": v(7.79, -15.24) * mm, "end": v(7.79, -20.11) * mm, "construction": true});
            skLineSegment(sketch, "E272", {"start": v(8.94, -14.6) * mm, "end": v(8.94, -19.63) * mm, "construction": true});
            skLineSegment(sketch, "E273", {"start": v(-8.94, -19.63) * mm, "end": v(-8.94, -22.43) * mm, "construction": true});
            skLineSegment(sketch, "E274", {"start": v(8.94, -19.63) * mm, "end": v(8.94, -22.43) * mm, "construction": true});
            skPoint(sketch, "E275", {"position": v(0, -26.25) * mm});
            skPoint(sketch, "E276.visualSharp", {"position": v(0, -30.25) * mm});
            skPoint(sketch, "E277", {"position": v(0, -24.5) * mm});
            skLineSegment(sketch, "E278", {"start": v(0, -26.25) * mm, "end": v(-11.25, -26.25) * mm, "construction": true});
            skLineSegment(sketch, "E279", {"start": v(0, -26.25) * mm, "end": v(11.25, -26.25) * mm, "construction": true});
            skPoint(sketch, "E280.visualSharp", {"position": v(-11.25, -26.25) * mm});
            skPoint(sketch, "E281.visualSharp", {"position": v(11.25, -26.25) * mm});
            skPoint(sketch, "E282.visualSharp", {"position": v(0, -37.76) * mm});
            skPoint(sketch, "E283", {"position": v(0, -39.7) * mm});
            skLineSegment(sketch, "E284", {"start": v(-9.19, -28.72) * mm, "end": v(-1.34, -38.1) * mm});
            skLineSegment(sketch, "E285", {"start": v(1.34, -38.1) * mm, "end": v(9.19, -28.72) * mm});
            skLineSegment(sketch, "E286", {"start": v(-8.04, -26.25) * mm, "end": v(8.04, -26.25) * mm});
            skArc(sketch, "E287.filletArc", {"start": v(-8.04, -26.25) * mm, "mid": v(-9.4, -27.12) * mm, "end": v(-9.19, -28.72) * mm});
            skArc(sketch, "E288.filletArc", {"start": v(9.19, -28.72) * mm, "mid": v(9.4, -27.12) * mm, "end": v(8.04, -26.25) * mm});
            skArc(sketch, "E289.filletArc", {"start": v(-1.34, -38.1) * mm, "mid": v(0, -38.72) * mm, "end": v(1.34, -38.1) * mm});
            skLineSegment(sketch, "E290", {"start": v(0, 34) * mm, "end": v(8.73, 34) * mm, "construction": true});
            skLineSegment(sketch, "E291", {"start": v(0, 34) * mm, "end": v(-8.73, 34) * mm, "construction": true});
            skLineSegment(sketch, "E292", {"start": v(11.5, 31.26) * mm, "end": v(0, 31.26) * mm, "construction": true});
            skLineSegment(sketch, "E293", {"start": v(0, 31.26) * mm, "end": v(0, 50.76) * mm, "construction": true});
            skLineSegment(sketch, "E294", {"start": v(0, 50.76) * mm, "end": v(0, 63.06) * mm, "construction": true});
            skLineSegment(sketch, "E295", {"start": v(0, 63.06) * mm, "end": v(6.75, 63.06) * mm, "construction": true});
            skSolve(sketch);
        }
        {
            var Q0;
            Q0=qCreatedBy(makeId("Top.planeOp"),FACE);
            var sketch = newSketch(context, id + "F1", { "sketchPlane" : qUnion([Q0])});
            skLineSegment(sketch, "E296.bottom", {"start": v(-15.24, 15.25) * mm, "end": v(15.26, 15.25) * mm, "construction": true});
            skLineSegment(sketch, "E296.top", {"start": v(-15.24, -15.25) * mm, "end": v(15.26, -15.25) * mm, "construction": true});
            skLineSegment(sketch, "E296.left", {"start": v(-15.24, 15.25) * mm, "end": v(-15.24, -15.25) * mm, "construction": true});
            skLineSegment(sketch, "E296.right", {"start": v(15.26, 15.25) * mm, "end": v(15.26, -15.25) * mm, "construction": true});
            skPoint(sketch, "E296.middle", {"position": v(0, 0) * mm});
            skLineSegment(sketch, "E297.bottom", {"start": v(30.26, 30.25) * mm, "end": v(-30.24, 30.25) * mm, "construction": true});
            skLineSegment(sketch, "E297.top", {"start": v(30.26, -30.25) * mm, "end": v(-30.24, -30.25) * mm, "construction": true});
            skLineSegment(sketch, "E297.left", {"start": v(30.26, 30.25) * mm, "end": v(30.26, -30.25) * mm, "construction": true});
            skLineSegment(sketch, "E297.right", {"start": v(-30.24, 30.25) * mm, "end": v(-30.24, -30.25) * mm, "construction": true});
            skLineSegment(sketch, "E298.bottom", {"start": v(-82.5, 82.5) * mm, "end": v(82.5, 82.5) * mm, "construction": true});
            skLineSegment(sketch, "E298.top", {"start": v(-82.5, -82.5) * mm, "end": v(82.5, -82.5) * mm, "construction": true});
            skLineSegment(sketch, "E298.left", {"start": v(-82.5, 82.5) * mm, "end": v(-82.5, -82.5) * mm, "construction": true});
            skLineSegment(sketch, "E298.right", {"start": v(82.5, 82.5) * mm, "end": v(82.5, -82.5) * mm, "construction": true});
            skCircle(sketch, "E299", {"center": v(82.5, 82.5) * mm, "radius": 4.5 * mm});
            skCircle(sketch, "E300", {"center": v(-82.5, 82.5) * mm, "radius": 4.5 * mm, "construction": true});
            skCircle(sketch, "E301", {"center": v(82.5, -82.5) * mm, "radius": 4.5 * mm, "construction": true});
            skCircle(sketch, "E302", {"center": v(-82.5, -82.5) * mm, "radius": 4.5 * mm, "construction": true});
            skCircle(sketch, "E303", {"center": v(82.5, 82.5) * mm, "radius": 8 * mm, "construction": true});
            skCircle(sketch, "E304", {"center": v(82.5, -82.5) * mm, "radius": 8 * mm, "construction": true});
            skCircle(sketch, "E305", {"center": v(-82.5, -82.5) * mm, "radius": 8 * mm, "construction": true});
            skCircle(sketch, "E306", {"center": v(-82.5, 82.5) * mm, "radius": 8 * mm, "construction": true});
            skCircle(sketch, "E307", {"center": v(82.5, 82.5) * mm, "radius": 9.5 * mm, "construction": true});
            skCircle(sketch, "E308", {"center": v(82.5, -82.5) * mm, "radius": 9.5 * mm, "construction": true});
            skCircle(sketch, "E309", {"center": v(-82.5, -82.5) * mm, "radius": 9.5 * mm, "construction": true});
            skCircle(sketch, "E310", {"center": v(-82.5, 82.5) * mm, "radius": 9.5 * mm, "construction": true});
            skCircle(sketch, "E311", {"center": v(82.5, 82.5) * mm, "radius": 14 * mm, "construction": true});
            skCircle(sketch, "E312", {"center": v(-82.5, 82.5) * mm, "radius": 14 * mm, "construction": true});
            skCircle(sketch, "E313", {"center": v(82.5, -82.5) * mm, "radius": 14 * mm, "construction": true});
            skCircle(sketch, "E314", {"center": v(-82.5, -82.5) * mm, "radius": 14 * mm, "construction": true});
            skCircle(sketch, "E315", {"center": v(82.5, 82.5) * mm, "radius": 63.5 * mm, "construction": true});
            skCircle(sketch, "E316", {"center": v(82.5, -82.5) * mm, "radius": 63.5 * mm, "construction": true});
            skCircle(sketch, "E317", {"center": v(-82.5, -82.5) * mm, "radius": 63.5 * mm, "construction": true});
            skCircle(sketch, "E318", {"center": v(-82.5, 82.5) * mm, "radius": 63.5 * mm, "construction": true});
            skLineSegment(sketch, "E319", {"start": v(0, 30.25) * mm, "end": v(0, 36.4) * mm, "construction": true});
            skLineSegment(sketch, "E320", {"start": v(0, 36.4) * mm, "end": v(-14.28, 36.4) * mm, "construction": true});
            skLineSegment(sketch, "E321", {"start": v(0, 36.4) * mm, "end": v(14.3, 36.4) * mm, "construction": true});
            skLineSegment(sketch, "E322", {"start": v(0, -30.25) * mm, "end": v(0, -36.4) * mm, "construction": true});
            skLineSegment(sketch, "E323", {"start": v(0, -36.4) * mm, "end": v(-14.28, -36.4) * mm, "construction": true});
            skLineSegment(sketch, "E324", {"start": v(0, -36.4) * mm, "end": v(14.3, -36.4) * mm, "construction": true});
            skLineSegment(sketch, "E325.bottom", {"start": v(-26.18, 26.2) * mm, "end": v(26.2, 26.2) * mm, "construction": true});
            skLineSegment(sketch, "E325.top", {"start": v(-26.18, -26.19) * mm, "end": v(26.2, -26.19) * mm, "construction": true});
            skLineSegment(sketch, "E325.left", {"start": v(-26.18, 26.2) * mm, "end": v(-26.18, -26.19) * mm, "construction": true});
            skLineSegment(sketch, "E325.right", {"start": v(26.2, 26.2) * mm, "end": v(26.2, -26.19) * mm, "construction": true});
            skCircle(sketch, "E326", {"center": v(30.26, 30.25) * mm, "radius": 7.5 * mm, "construction": true});
            skCircle(sketch, "E327", {"center": v(-30.24, 30.25) * mm, "radius": 7.5 * mm, "construction": true});
            skCircle(sketch, "E328", {"center": v(30.26, -30.25) * mm, "radius": 7.5 * mm, "construction": true});
            skCircle(sketch, "E329", {"center": v(-30.24, -30.25) * mm, "radius": 7.5 * mm, "construction": true});
            skCircle(sketch, "E330", {"center": v(15.26, 15.25) * mm, "radius": 1.5 * mm, "construction": true});
            skCircle(sketch, "E331", {"center": v(-15.24, 15.25) * mm, "radius": 1.5 * mm, "construction": true});
            skCircle(sketch, "E332", {"center": v(15.26, -15.25) * mm, "radius": 1.5 * mm, "construction": true});
            skCircle(sketch, "E333", {"center": v(-15.24, -15.25) * mm, "radius": 1.5 * mm, "construction": true});
            skLineSegment(sketch, "E334", {"start": v(15.26, 15.25) * mm, "end": v(0, 0) * mm, "construction": true});
            skLineSegment(sketch, "E335", {"start": v(-15.24, 15.25) * mm, "end": v(0, 0) * mm, "construction": true});
            skLineSegment(sketch, "E336", {"start": v(15.26, -15.25) * mm, "end": v(0, 0) * mm, "construction": true});
            skLineSegment(sketch, "E337", {"start": v(-15.24, -15.25) * mm, "end": v(0, 0) * mm, "construction": true});
            skCircle(sketch, "E338", {"center": v(15.26, 15.25) * mm, "radius": 5 * mm, "construction": true});
            skCircle(sketch, "E339", {"center": v(-15.24, 15.25) * mm, "radius": 5 * mm, "construction": true});
            skCircle(sketch, "E340", {"center": v(-15.24, -15.25) * mm, "radius": 5 * mm, "construction": true});
            skCircle(sketch, "E341", {"center": v(15.26, -15.25) * mm, "radius": 5 * mm, "construction": true});
            skLineSegment(sketch, "E342.bottom", {"start": v(-5.65, -5.65) * mm, "end": v(5.66, -5.65) * mm, "construction": true});
            skLineSegment(sketch, "E342.top", {"start": v(-5.65, 5.66) * mm, "end": v(5.66, 5.66) * mm, "construction": true});
            skLineSegment(sketch, "E342.left", {"start": v(-5.65, -5.65) * mm, "end": v(-5.65, 5.66) * mm, "construction": true});
            skLineSegment(sketch, "E342.right", {"start": v(5.66, -5.65) * mm, "end": v(5.66, 5.66) * mm, "construction": true});
            skPoint(sketch, "E343", {"position": v(0, 5.66) * mm});
            skPoint(sketch, "E344", {"position": v(5.66, 0) * mm});
            skPoint(sketch, "E345", {"position": v(-5.65, 0) * mm});
            skPoint(sketch, "E346", {"position": v(0, -5.65) * mm});
            skLineSegment(sketch, "E347", {"start": v(15.26, 15.25) * mm, "end": v(82.5, 82.5) * mm, "construction": true});
            skLineSegment(sketch, "E348", {"start": v(72.6, 72.6) * mm, "end": v(69.07, 76.14) * mm, "construction": true});
            skLineSegment(sketch, "E349", {"start": v(72.6, 72.6) * mm, "end": v(76.15, 69.06) * mm, "construction": true});
            skCircle(sketch, "E350", {"center": v(82.5, 82.5) * mm, "radius": 23.5 * mm, "construction": true});
            skLineSegment(sketch, "E351", {"start": v(82.5, 82.5) * mm, "end": v(82.5, 106) * mm, "construction": true});
            skLineSegment(sketch, "E352", {"start": v(82.5, 82.5) * mm, "end": v(106, 82.5) * mm, "construction": true});
            skCircle(sketch, "E353", {"center": v(82.5, 82.5) * mm, "radius": 15.5 * mm, "construction": true});
            skLineSegment(sketch, "E354", {"start": v(82.5, 82.5) * mm, "end": v(65.9, 99.12) * mm, "construction": true});
            skLineSegment(sketch, "E355", {"start": v(82.5, 82.5) * mm, "end": v(99.13, 65.88) * mm, "construction": true});
            skLineSegment(sketch, "E356", {"start": v(82.5, 82.5) * mm, "end": v(99.13, 99.12) * mm, "construction": true});
            skLineSegment(sketch, "E357", {"start": v(99.13, 65.88) * mm, "end": v(104.53, 74.3) * mm, "construction": true});
            skLineSegment(sketch, "E358", {"start": v(99.13, 99.12) * mm, "end": v(102.27, 95.23) * mm, "construction": true});
            skLineSegment(sketch, "E359", {"start": v(99.13, 99.12) * mm, "end": v(95.23, 102.26) * mm, "construction": true});
            skLineSegment(sketch, "E360", {"start": v(65.9, 99.12) * mm, "end": v(74.3, 104.52) * mm, "construction": true});
            skCircle(sketch, "E361", {"center": v(82.5, 82.5) * mm, "radius": 20 * mm, "construction": true});
            skLineSegment(sketch, "E362", {"start": v(74.3, 104.52) * mm, "end": v(76.25, 101.5) * mm, "construction": true});
            skLineSegment(sketch, "E363", {"start": v(95.23, 102.26) * mm, "end": v(93.02, 99.51) * mm, "construction": true});
            skLineSegment(sketch, "E364", {"start": v(102.27, 95.23) * mm, "end": v(99.52, 93.01) * mm, "construction": true});
            skPoint(sketch, "E365", {"position": v(68.37, 96.64) * mm});
            skPoint(sketch, "E366", {"position": v(70.1, 101.82) * mm});
            skLineSegment(sketch, "E367", {"start": v(76.25, 101.5) * mm, "end": v(93.02, 99.51) * mm, "construction": true});
            skLineSegment(sketch, "E368", {"start": v(84.64, 100.5) * mm, "end": v(84.33, 97.9) * mm, "construction": true});
            skLineSegment(sketch, "E369", {"start": v(84.33, 97.9) * mm, "end": v(84.15, 96.4) * mm, "construction": true});
            skPoint(sketch, "E370", {"position": v(101.83, 70.09) * mm});
            skLineSegment(sketch, "E371", {"start": v(104.53, 74.3) * mm, "end": v(101.5, 76.24) * mm, "construction": true});
            skPoint(sketch, "E372", {"position": v(96.65, 68.36) * mm});
            skPoint(sketch, "E373.visualSharp", {"position": v(68.5, 82.5) * mm});
            skPoint(sketch, "E374.visualSharp", {"position": v(84.15, 96.4) * mm});
            skPoint(sketch, "E375.visualSharp", {"position": v(96.5, 82.5) * mm});
            skPoint(sketch, "E376.visualSharp", {"position": v(82.5, 68.38) * mm});
            skPoint(sketch, "E377.visualSharp", {"position": v(69.07, 76.14) * mm});
            skPoint(sketch, "E378.visualSharp", {"position": v(76.15, 69.06) * mm});
            skLineSegment(sketch, "E379", {"start": v(88.17, 88.16) * mm, "end": v(91.35, 91.34) * mm, "construction": true});
            skLineSegment(sketch, "E380", {"start": v(82.5, 101.8) * mm, "end": v(77.26, 101.8) * mm, "construction": true});
            skLineSegment(sketch, "E381", {"start": v(82.5, 101.8) * mm, "end": v(87.76, 101.8) * mm, "construction": true});
            skFitSpline(sketch, "E382", {"points": [v(77.26, 101.8) * mm, v(82.5, 106) * mm, v(87.76, 101.8) * mm], "startDerivative": vector(9, 14.06) * mm, "endDerivative": vector(9, -14.06) * mm});
            skLineSegment(sketch, "E383", {"start": v(82.5, 104.14) * mm, "end": v(86.26, 104.14) * mm, "construction": true});
            skLineSegment(sketch, "E384", {"start": v(82.5, 104.14) * mm, "end": v(78.76, 104.14) * mm, "construction": true});
            skLineSegment(sketch, "E385", {"start": v(77.26, 101.8) * mm, "end": v(72.6, 92.4) * mm});
            skPoint(sketch, "E386", {"position": v(69.48, 87.63) * mm});
            skArc(sketch, "E387", {"start": v(72.6, 92.4) * mm, "mid": v(69.58, 87.86) * mm, "end": v(68.5, 82.5) * mm});
            skPoint(sketch, "E388", {"position": v(95.63, 87.39) * mm});
            skFitSpline(sketch, "E389", {"points": [v(95.63, 87.39) * mm, v(102.5, 82.5) * mm, v(80.03, 67.2) * mm], "startDerivative": vector(24.48, -10.1) * mm, "endDerivative": vector(-49.92, -7.72) * mm});
            skLineSegment(sketch, "E390", {"start": v(16.8, 16.8) * mm, "end": v(13.62, 19.97) * mm, "construction": true});
            skLineSegment(sketch, "E391", {"start": v(16.8, 16.8) * mm, "end": v(19.98, 13.6) * mm, "construction": true});
            skLineSegment(sketch, "E392", {"start": v(37.75, 30.67) * mm, "end": v(29.84, 22.76) * mm, "construction": true});
            skLineSegment(sketch, "E393", {"start": v(30.68, 37.74) * mm, "end": v(22.83, 31.31) * mm, "construction": true});
            skLineSegment(sketch, "E394", {"start": v(22.83, 31.31) * mm, "end": v(13.62, 19.97) * mm});
            skLineSegment(sketch, "E395", {"start": v(29.84, 22.76) * mm, "end": v(19.98, 13.6) * mm});
            skPoint(sketch, "E396", {"position": v(25.01, 35.61) * mm});
            skPoint(sketch, "E397", {"position": v(35.69, 25.07) * mm});
            skArc(sketch, "E398", {"start": v(29.84, 22.76) * mm, "mid": v(34.71, 24.21) * mm, "end": v(37.54, 28.44) * mm});
            skArc(sketch, "E399", {"start": v(28.45, 37.53) * mm, "mid": v(24.7, 35.27) * mm, "end": v(22.83, 31.31) * mm});
            skLineSegment(sketch, "E400.bottom", {"start": v(0, 5.66) * mm, "end": v(6.37, 5.66) * mm, "construction": true});
            skLineSegment(sketch, "E400.top", {"start": v(0, 12.02) * mm, "end": v(6.37, 12.02) * mm, "construction": true});
            skLineSegment(sketch, "E400.left", {"start": v(0, 5.66) * mm, "end": v(0, 12.02) * mm, "construction": true});
            skLineSegment(sketch, "E400.right", {"start": v(6.37, 5.66) * mm, "end": v(6.37, 12.02) * mm, "construction": true});
            skLineSegment(sketch, "E401", {"start": v(0, 5.66) * mm, "end": v(6.37, 12.02) * mm});
            skLineSegment(sketch, "E402", {"start": v(6.37, 12.02) * mm, "end": v(10.3, 15.95) * mm});
            skLineSegment(sketch, "E403.bottom", {"start": v(5.66, 0) * mm, "end": v(12.02, 0) * mm, "construction": true});
            skLineSegment(sketch, "E403.top", {"start": v(5.66, 6.36) * mm, "end": v(12.02, 6.36) * mm, "construction": true});
            skLineSegment(sketch, "E403.left", {"start": v(5.66, 0) * mm, "end": v(5.66, 6.36) * mm, "construction": true});
            skLineSegment(sketch, "E403.right", {"start": v(12.02, 0) * mm, "end": v(12.02, 6.36) * mm, "construction": true});
            skLineSegment(sketch, "E404", {"start": v(5.66, 0) * mm, "end": v(12.02, 6.36) * mm});
            skLineSegment(sketch, "E405", {"start": v(12.02, 6.36) * mm, "end": v(15.96, 10.3) * mm});
            skPoint(sketch, "E406", {"position": v(11.75, 18.81) * mm});
            skPoint(sketch, "E407", {"position": v(19.05, 11.99) * mm});
            skArc(sketch, "E408", {"start": v(15.96, 10.3) * mm, "mid": v(18.44, 11.4) * mm, "end": v(19.98, 13.6) * mm});
            skArc(sketch, "E409", {"start": v(13.62, 19.97) * mm, "mid": v(11.4, 18.43) * mm, "end": v(10.3, 15.95) * mm});
            skLineSegment(sketch, "E410", {"start": v(0, 5.66) * mm, "end": v(0, 0) * mm});
            skLineSegment(sketch, "E411", {"start": v(0, 0) * mm, "end": v(5.66, 0) * mm});
            skCircle(sketch, "E412", {"center": v(30.26, 30.25) * mm, "radius": 1.5 * mm});
            skCircle(sketch, "E413", {"center": v(15.26, 15.25) * mm, "radius": 1.5 * mm});
            skPoint(sketch, "E414", {"position": v(82.5, 102.5) * mm});
            skLineSegment(sketch, "E415", {"start": v(82.5, 98) * mm, "end": v(78.84, 97.56) * mm, "construction": true});
            skLineSegment(sketch, "E416", {"start": v(82.5, 98) * mm, "end": v(86.18, 97.56) * mm, "construction": true});
            skLineSegment(sketch, "E417", {"start": v(86.18, 97.56) * mm, "end": v(87.35, 95.64) * mm, "construction": true});
            skLineSegment(sketch, "E418", {"start": v(78.84, 97.56) * mm, "end": v(77.67, 95.64) * mm, "construction": true});
            skPoint(sketch, "E419", {"position": v(87.35, 95.64) * mm});
            skPoint(sketch, "E420", {"position": v(77.67, 95.64) * mm});
            skPoint(sketch, "E421", {"position": v(82.5, 100.76) * mm});
            skLineSegment(sketch, "E422", {"start": v(78.84, 97.56) * mm, "end": v(79.02, 96.06) * mm, "construction": true});
            skLineSegment(sketch, "E423", {"start": v(86.18, 97.56) * mm, "end": v(86, 96.06) * mm, "construction": true});
            skLineSegment(sketch, "E424", {"start": v(79.02, 96.06) * mm, "end": v(79.14, 95.06) * mm, "construction": true});
            skLineSegment(sketch, "E425", {"start": v(86, 96.06) * mm, "end": v(85.88, 95.06) * mm, "construction": true});
            skFitSpline(sketch, "E426", {"points": [v(79.02, 96.06) * mm, v(82.5, 100.76) * mm, v(86, 96.06) * mm], "startDerivative": vector(6.99, 14.1) * mm, "endDerivative": vector(6.99, -14.1) * mm});
            skLineSegment(sketch, "E427", {"start": v(79.14, 95.06) * mm, "end": v(85.88, 95.06) * mm, "construction": true});
            skPoint(sketch, "E428", {"position": v(82.5, 95.06) * mm});
            skFitSpline(sketch, "E429", {"points": [v(79.02, 96.06) * mm, v(82.5, 95.06) * mm, v(86, 96.06) * mm], "startDerivative": vector(0.72, -5.96) * mm, "endDerivative": vector(0.72, 5.96) * mm});
            skCircle(sketch, "E430", {"center": v(82.5, 90.5) * mm, "radius": 1.5 * mm, "construction": true});
            skCircle(sketch, "E431", {"center": v(82.5, 92) * mm, "radius": 1.5 * mm, "construction": true});
            skCircle(sketch, "E432", {"center": v(90.5, 82.5) * mm, "radius": 1.5 * mm, "construction": true});
            skCircle(sketch, "E433", {"center": v(92, 82.5) * mm, "radius": 1.5 * mm, "construction": true});
            skCircle(sketch, "E434", {"center": v(82.5, 74.5) * mm, "radius": 1.5 * mm, "construction": true});
            skCircle(sketch, "E435", {"center": v(82.5, 73) * mm, "radius": 1.5 * mm, "construction": true});
            skCircle(sketch, "E436", {"center": v(74.5, 82.5) * mm, "radius": 1.5 * mm, "construction": true});
            skCircle(sketch, "E437", {"center": v(73, 82.5) * mm, "radius": 1.5 * mm, "construction": true});
            skPoint(sketch, "E438", {"position": v(83.8, 91.25) * mm});
            skPoint(sketch, "E439", {"position": v(81.21, 91.25) * mm});
            skPoint(sketch, "E440", {"position": v(82.5, 93.5) * mm});
            skPoint(sketch, "E441", {"position": v(82.5, 89) * mm});
            skArc(sketch, "E442", {"start": v(81.21, 91.25) * mm, "mid": v(82.5, 89) * mm, "end": v(83.8, 91.25) * mm});
            skArc(sketch, "E443", {"start": v(83.8, 91.25) * mm, "mid": v(82.5, 93.5) * mm, "end": v(81.21, 91.25) * mm});
            skPoint(sketch, "E444", {"position": v(89, 82.5) * mm});
            skPoint(sketch, "E445", {"position": v(91.26, 83.8) * mm});
            skPoint(sketch, "E446", {"position": v(91.26, 81.2) * mm});
            skPoint(sketch, "E447", {"position": v(93.5, 82.5) * mm});
            skPoint(sketch, "E448", {"position": v(82.5, 71.5) * mm});
            skPoint(sketch, "E449", {"position": v(82.5, 76) * mm});
            skPoint(sketch, "E450", {"position": v(81.21, 73.75) * mm});
            skPoint(sketch, "E451", {"position": v(83.8, 73.75) * mm});
            skPoint(sketch, "E452", {"position": v(73.76, 83.8) * mm});
            skPoint(sketch, "E453", {"position": v(73.76, 81.2) * mm});
            skPoint(sketch, "E454", {"position": v(71.5, 82.5) * mm});
            skPoint(sketch, "E455", {"position": v(76, 82.5) * mm});
            skArc(sketch, "E456", {"start": v(73.76, 81.2) * mm, "mid": v(76, 82.5) * mm, "end": v(73.76, 83.8) * mm});
            skArc(sketch, "E457", {"start": v(73.76, 83.8) * mm, "mid": v(71.5, 82.5) * mm, "end": v(73.76, 81.2) * mm});
            skArc(sketch, "E458", {"start": v(91.26, 83.8) * mm, "mid": v(89, 82.5) * mm, "end": v(91.26, 81.2) * mm});
            skArc(sketch, "E459", {"start": v(91.26, 81.2) * mm, "mid": v(93.5, 82.5) * mm, "end": v(91.26, 83.8) * mm});
            skArc(sketch, "E460", {"start": v(81.21, 73.75) * mm, "mid": v(82.5, 71.5) * mm, "end": v(83.8, 73.75) * mm});
            skArc(sketch, "E461", {"start": v(83.8, 73.75) * mm, "mid": v(82.5, 76) * mm, "end": v(81.21, 73.75) * mm});
            skLineSegment(sketch, "E462", {"start": v(87.76, 101.8) * mm, "end": v(92.4, 92.4) * mm});
            skPoint(sketch, "E463", {"position": v(94.28, 90.08) * mm});
            skArc(sketch, "E464", {"start": v(95.63, 87.39) * mm, "mid": v(94.29, 90.07) * mm, "end": v(92.4, 92.4) * mm});
            skPoint(sketch, "E465", {"position": v(96.49, 83.32) * mm});
            skPoint(sketch, "E466", {"position": v(98, 82.5) * mm});
            skPoint(sketch, "E467", {"position": v(72.22, 82.5) * mm});
            skCircle(sketch, "E468", {"center": v(82.5, 82.5) * mm, "radius": 76.2 * mm, "construction": true});
            skCircle(sketch, "E469", {"center": v(-82.5, 82.5) * mm, "radius": 76.2 * mm, "construction": true});
            skCircle(sketch, "E470", {"center": v(-82.5, -82.5) * mm, "radius": 76.2 * mm, "construction": true});
            skCircle(sketch, "E471", {"center": v(82.5, -82.5) * mm, "radius": 76.2 * mm, "construction": true});
            skFitSpline(sketch, "E472", {"points": [v(96.49, 83.32) * mm, v(98, 82.5) * mm, v(94.18, 76.07) * mm], "startDerivative": vector(6.57, -0.64) * mm, "endDerivative": vector(-10.5, -9.19) * mm});
            skPoint(sketch, "E473", {"position": v(95.46, 82.5) * mm});
            skFitSpline(sketch, "E474", {"points": [v(96.49, 83.32) * mm, v(95.46, 82.5) * mm, v(94.18, 76.07) * mm], "startDerivative": vector(-5.8, 0.38) * mm, "endDerivative": vector(7.44, 8.28) * mm});
            skLineSegment(sketch, "E475", {"start": v(33.1, 40.16) * mm, "end": v(64.62, 71.68) * mm});
            skFitSpline(sketch, "E476", {"points": [v(64.62, 71.68) * mm, v(68.5, 82.5) * mm], "startDerivative": vector(7.91, 8.8) * mm, "endDerivative": vector(0.5, 11.46) * mm});
            skLineSegment(sketch, "E477", {"start": v(62.79, 62.78) * mm, "end": v(59.25, 66.31) * mm, "construction": true});
            skPoint(sketch, "E478.visualSharp", {"position": v(30.68, 37.74) * mm});
            skArc(sketch, "E478.filletArc", {"start": v(28.45, 37.53) * mm, "mid": v(30.95, 38.53) * mm, "end": v(33.1, 40.16) * mm});
            skPoint(sketch, "E479.visualSharp", {"position": v(37.75, 30.67) * mm});
            skArc(sketch, "E479.filletArc", {"start": v(40.17, 33.09) * mm, "mid": v(38.54, 30.94) * mm, "end": v(37.54, 28.44) * mm});
            skLineSegment(sketch, "E480", {"start": v(40.17, 33.09) * mm, "end": v(71.68, 64.6) * mm});
            skFitSpline(sketch, "E481", {"points": [v(71.68, 64.6) * mm, v(80.03, 67.2) * mm], "startDerivative": vector(10.6, 9.53) * mm, "endDerivative": vector(7.58, 1.8) * mm});
            skSolve(sketch);
        }
        {
            var Q0;
            Q0=qSketchRegion(id+"F0",true);
            extrude(context, id + "F2", {"entities" : qUnion([Q0]), "depth" : 2 * mm});
        }
        {
            var Q0;
            Q0=qCreatedBy(makeId("Top.planeOp"),FACE);
            var sketch = newSketch(context, id + "F3", { "sketchPlane" : qUnion([Q0])});
            skLineSegment(sketch, "E482.bottom", {"start": v(-15.25, 15.25) * mm, "end": v(15.25, 15.25) * mm, "construction": true});
            skLineSegment(sketch, "E482.top", {"start": v(-15.25, -15.25) * mm, "end": v(15.25, -15.25) * mm, "construction": true});
            skLineSegment(sketch, "E482.left", {"start": v(-15.25, 15.25) * mm, "end": v(-15.25, -15.25) * mm, "construction": true});
            skLineSegment(sketch, "E482.right", {"start": v(15.25, 15.25) * mm, "end": v(15.25, -15.25) * mm, "construction": true});
            skPoint(sketch, "E482.middle", {"position": v(0, 0) * mm});
            skLineSegment(sketch, "E483.bottom", {"start": v(30.25, 30.25) * mm, "end": v(-30.25, 30.25) * mm, "construction": true});
            skLineSegment(sketch, "E483.top", {"start": v(30.25, -30.25) * mm, "end": v(-30.25, -30.25) * mm, "construction": true});
            skLineSegment(sketch, "E483.left", {"start": v(30.25, 30.25) * mm, "end": v(30.25, -30.25) * mm, "construction": true});
            skLineSegment(sketch, "E483.right", {"start": v(-30.25, 30.25) * mm, "end": v(-30.25, -30.25) * mm, "construction": true});
            skLineSegment(sketch, "E484.bottom", {"start": v(-70.96, 70.96) * mm, "end": v(70.96, 70.96) * mm, "construction": true});
            skLineSegment(sketch, "E484.top", {"start": v(-70.96, -70.96) * mm, "end": v(70.96, -70.96) * mm, "construction": true});
            skLineSegment(sketch, "E484.left", {"start": v(-70.96, 70.96) * mm, "end": v(-70.96, -70.96) * mm, "construction": true});
            skLineSegment(sketch, "E484.right", {"start": v(70.96, 70.96) * mm, "end": v(70.96, -70.96) * mm, "construction": true});
            skCircle(sketch, "E485", {"center": v(70.96, 70.96) * mm, "radius": 4.5 * mm, "construction": true});
            skCircle(sketch, "E486", {"center": v(-70.96, 70.96) * mm, "radius": 4.5 * mm, "construction": true});
            skCircle(sketch, "E487", {"center": v(70.96, -70.96) * mm, "radius": 4.5 * mm, "construction": true});
            skCircle(sketch, "E488", {"center": v(-70.96, -70.96) * mm, "radius": 4.5 * mm, "construction": true});
            skCircle(sketch, "E489", {"center": v(70.96, 70.96) * mm, "radius": 8 * mm, "construction": true});
            skCircle(sketch, "E490", {"center": v(70.96, -70.96) * mm, "radius": 8 * mm, "construction": true});
            skCircle(sketch, "E491", {"center": v(-70.96, -70.96) * mm, "radius": 8 * mm, "construction": true});
            skCircle(sketch, "E492", {"center": v(-70.96, 70.96) * mm, "radius": 8 * mm, "construction": true});
            skCircle(sketch, "E493", {"center": v(70.96, 70.96) * mm, "radius": 9.5 * mm, "construction": true});
            skCircle(sketch, "E494", {"center": v(70.96, -70.96) * mm, "radius": 9.5 * mm, "construction": true});
            skCircle(sketch, "E495", {"center": v(-70.96, -70.96) * mm, "radius": 9.5 * mm, "construction": true});
            skCircle(sketch, "E496", {"center": v(-70.96, 70.96) * mm, "radius": 9.5 * mm, "construction": true});
            skCircle(sketch, "E497", {"center": v(70.96, 70.96) * mm, "radius": 14 * mm, "construction": true});
            skCircle(sketch, "E498", {"center": v(-70.96, 70.96) * mm, "radius": 14 * mm, "construction": true});
            skCircle(sketch, "E499", {"center": v(70.96, -70.96) * mm, "radius": 14 * mm, "construction": true});
            skCircle(sketch, "E500", {"center": v(-70.96, -70.96) * mm, "radius": 14 * mm, "construction": true});
            skCircle(sketch, "E501", {"center": v(70.96, 70.96) * mm, "radius": 63.5 * mm, "construction": true});
            skCircle(sketch, "E502", {"center": v(70.96, -70.96) * mm, "radius": 63.5 * mm, "construction": true});
            skCircle(sketch, "E503", {"center": v(-70.96, -70.96) * mm, "radius": 63.5 * mm, "construction": true});
            skCircle(sketch, "E504", {"center": v(-70.96, 70.96) * mm, "radius": 63.5 * mm, "construction": true});
            skLineSegment(sketch, "E505", {"start": v(0, 30.25) * mm, "end": v(0, 36.4) * mm, "construction": true});
            skLineSegment(sketch, "E506", {"start": v(0, 36.4) * mm, "end": v(-14.3, 36.4) * mm, "construction": true});
            skLineSegment(sketch, "E507", {"start": v(0, 36.4) * mm, "end": v(14.29, 36.4) * mm, "construction": true});
            skLineSegment(sketch, "E508", {"start": v(0, -30.25) * mm, "end": v(0, -36.4) * mm, "construction": true});
            skLineSegment(sketch, "E509", {"start": v(0, -36.4) * mm, "end": v(-14.29, -36.4) * mm, "construction": true});
            skLineSegment(sketch, "E510", {"start": v(0, -36.4) * mm, "end": v(14.3, -36.4) * mm, "construction": true});
            skLineSegment(sketch, "E511.bottom", {"start": v(-26.2, 26.2) * mm, "end": v(26.2, 26.2) * mm, "construction": true});
            skLineSegment(sketch, "E511.top", {"start": v(-26.2, -26.19) * mm, "end": v(26.2, -26.19) * mm, "construction": true});
            skLineSegment(sketch, "E511.left", {"start": v(-26.2, 26.2) * mm, "end": v(-26.2, -26.19) * mm, "construction": true});
            skLineSegment(sketch, "E511.right", {"start": v(26.2, 26.2) * mm, "end": v(26.2, -26.2) * mm, "construction": true});
            skCircle(sketch, "E512", {"center": v(30.25, 30.25) * mm, "radius": 5 * mm, "construction": true});
            skCircle(sketch, "E513", {"center": v(-30.25, 30.25) * mm, "radius": 5 * mm, "construction": true});
            skCircle(sketch, "E514", {"center": v(30.25, -30.25) * mm, "radius": 5 * mm, "construction": true});
            skCircle(sketch, "E515", {"center": v(-30.25, -30.25) * mm, "radius": 5 * mm, "construction": true});
            skLineSegment(sketch, "E516", {"start": v(-26.19, 26.2) * mm, "end": v(-30.25, 30.25) * mm, "construction": true});
            skLineSegment(sketch, "E517", {"start": v(-26.71, 26.71) * mm, "end": v(-33.79, 33.79) * mm, "construction": true});
            skLineSegment(sketch, "E518", {"start": v(-31.46, 31.46) * mm, "end": v(-28.13, 34.78) * mm, "construction": true});
            skLineSegment(sketch, "E519", {"start": v(-31.46, 31.46) * mm, "end": v(-34.78, 28.13) * mm, "construction": true});
            skLineSegment(sketch, "E520", {"start": v(26.2, 26.2) * mm, "end": v(30.25, 30.25) * mm, "construction": true});
            skLineSegment(sketch, "E521", {"start": v(26.71, 26.71) * mm, "end": v(33.79, 33.79) * mm, "construction": true});
            skLineSegment(sketch, "E522", {"start": v(31.46, 31.46) * mm, "end": v(34.78, 28.13) * mm, "construction": true});
            skLineSegment(sketch, "E523", {"start": v(31.46, 31.46) * mm, "end": v(28.13, 34.78) * mm, "construction": true});
            skLineSegment(sketch, "E524", {"start": v(26.19, -26.19) * mm, "end": v(30.25, -30.25) * mm, "construction": true});
            skLineSegment(sketch, "E525", {"start": v(26.71, -26.71) * mm, "end": v(33.79, -33.79) * mm, "construction": true});
            skLineSegment(sketch, "E526", {"start": v(31.46, -31.46) * mm, "end": v(34.78, -28.13) * mm, "construction": true});
            skLineSegment(sketch, "E527", {"start": v(31.46, -31.46) * mm, "end": v(28.13, -34.78) * mm, "construction": true});
            skLineSegment(sketch, "E528", {"start": v(-26.2, -26.2) * mm, "end": v(-30.25, -30.25) * mm, "construction": true});
            skLineSegment(sketch, "E529", {"start": v(-26.71, -26.71) * mm, "end": v(-33.79, -33.79) * mm, "construction": true});
            skLineSegment(sketch, "E530", {"start": v(-31.46, -31.46) * mm, "end": v(-28.13, -34.78) * mm, "construction": true});
            skLineSegment(sketch, "E531", {"start": v(-31.46, -31.46) * mm, "end": v(-34.78, -28.13) * mm, "construction": true});
            skArc(sketch, "E532", {"start": v(-28.13, 34.78) * mm, "mid": v(-33.79, 33.79) * mm, "end": v(-34.78, 28.13) * mm});
            skArc(sketch, "E533", {"start": v(34.78, 28.13) * mm, "mid": v(33.79, 33.79) * mm, "end": v(28.13, 34.78) * mm});
            skArc(sketch, "E534", {"start": v(28.13, -34.78) * mm, "mid": v(33.79, -33.79) * mm, "end": v(34.78, -28.13) * mm});
            skArc(sketch, "E535", {"start": v(-34.78, -28.13) * mm, "mid": v(-33.79, -33.79) * mm, "end": v(-28.13, -34.78) * mm});
            skLineSegment(sketch, "E536.bottom", {"start": v(24.5, -24.5) * mm, "end": v(-24.5, -24.5) * mm, "construction": true});
            skLineSegment(sketch, "E536.top", {"start": v(24.5, 24.5) * mm, "end": v(-24.5, 24.5) * mm, "construction": true});
            skLineSegment(sketch, "E536.left", {"start": v(24.5, -24.5) * mm, "end": v(24.5, 24.5) * mm, "construction": true});
            skLineSegment(sketch, "E536.right", {"start": v(-24.5, -24.5) * mm, "end": v(-24.5, 24.5) * mm, "construction": true});
            skLineSegment(sketch, "E537", {"start": v(34.78, 28.13) * mm, "end": v(28.26, 10.3) * mm});
            skLineSegment(sketch, "E538", {"start": v(28.26, -10.3) * mm, "end": v(34.78, -28.13) * mm});
            skLineSegment(sketch, "E539", {"start": v(-34.78, -28.13) * mm, "end": v(-28.26, -10.3) * mm});
            skLineSegment(sketch, "E540", {"start": v(-28.26, 10.3) * mm, "end": v(-34.78, 28.13) * mm});
            skPoint(sketch, "E541.visualSharp", {"position": v(24.5, 0) * mm});
            skArc(sketch, "E541.filletArc", {"start": v(28.26, 10.3) * mm, "mid": v(26.44, 0) * mm, "end": v(28.26, -10.3) * mm});
            skPoint(sketch, "E542.visualSharp", {"position": v(-24.5, 0) * mm});
            skArc(sketch, "E542.filletArc", {"start": v(-28.26, -10.3) * mm, "mid": v(-26.44, 0) * mm, "end": v(-28.26, 10.3) * mm});
            skPoint(sketch, "E543.visualSharp", {"position": v(0, -24.5) * mm});
            skLineSegment(sketch, "E544", {"start": v(-28.13, 34.78) * mm, "end": v(-11.4, 23.17) * mm});
            skLineSegment(sketch, "E545", {"start": v(11.4, 23.17) * mm, "end": v(28.13, 34.78) * mm});
            skPoint(sketch, "E546.visualSharp", {"position": v(0, 15.25) * mm});
            skArc(sketch, "E546.filletArc", {"start": v(-11.4, 23.17) * mm, "mid": v(0, 19.6) * mm, "end": v(11.4, 23.17) * mm});
            skCircle(sketch, "E547", {"center": v(-30.25, 30.25) * mm, "radius": 1.5 * mm});
            skCircle(sketch, "E548", {"center": v(-15.25, 15.25) * mm, "radius": 1.5 * mm});
            skCircle(sketch, "E549", {"center": v(15.25, 15.25) * mm, "radius": 1.5 * mm});
            skCircle(sketch, "E550", {"center": v(30.25, 30.25) * mm, "radius": 1.5 * mm});
            skCircle(sketch, "E551", {"center": v(30.25, -30.25) * mm, "radius": 1.5 * mm});
            skCircle(sketch, "E552", {"center": v(15.25, -15.25) * mm, "radius": 1.5 * mm});
            skCircle(sketch, "E553", {"center": v(-15.25, -15.25) * mm, "radius": 1.5 * mm});
            skCircle(sketch, "E554", {"center": v(-30.25, -30.25) * mm, "radius": 1.5 * mm});
            skLineSegment(sketch, "E555", {"start": v(-28.13, -34.78) * mm, "end": v(-11.4, -23.17) * mm});
            skLineSegment(sketch, "E556", {"start": v(11.4, -23.17) * mm, "end": v(28.13, -34.78) * mm});
            skPoint(sketch, "E557.visualSharp", {"position": v(0, -15.25) * mm});
            skArc(sketch, "E557.filletArc", {"start": v(11.4, -23.17) * mm, "mid": v(0, -19.6) * mm, "end": v(-11.4, -23.17) * mm});
            skSolve(sketch);
        }
        {
            var Q0;
            Q0=qSketchRegion(id+"F1",true);
            extrude(context, id + "F4", {"entities" : qUnion([Q0]), "operationType" : NewBodyOperationType.ADD, "depth" : 7 * mm, "hasSecondDirection" : true, "secondDirectionOppositeDirection" : false, "secondDirectionDepth" : 3 * mm});
        }
        {
            var Q0;
            Q0=qCreatedBy(makeId("Top.planeOp"),FACE);
            var sketch = newSketch(context, id + "F5", { "sketchPlane" : qUnion([Q0])});
            skLineSegment(sketch, "E558.bottom", {"start": v(-15.28, 17.52) * mm, "end": v(15.22, 17.52) * mm, "construction": true});
            skLineSegment(sketch, "E558.top", {"start": v(-15.25, -12.98) * mm, "end": v(15.25, -12.98) * mm, "construction": true});
            skLineSegment(sketch, "E558.left", {"start": v(-15.25, 17.52) * mm, "end": v(-15.25, -12.98) * mm, "construction": true});
            skLineSegment(sketch, "E558.right", {"start": v(15.22, 17.52) * mm, "end": v(15.22, -12.98) * mm, "construction": true});
            skPoint(sketch, "E558.middle", {"position": v(-0.01, 2.27) * mm});
            skLineSegment(sketch, "E559.bottom", {"start": v(30.24, 32.52) * mm, "end": v(-30.26, 32.52) * mm, "construction": true});
            skLineSegment(sketch, "E559.top", {"start": v(30.24, -27.98) * mm, "end": v(-30.26, -27.98) * mm, "construction": true});
            skLineSegment(sketch, "E559.left", {"start": v(30.24, 32.52) * mm, "end": v(30.24, -27.98) * mm, "construction": true});
            skLineSegment(sketch, "E559.right", {"start": v(-30.26, 32.52) * mm, "end": v(-30.26, -27.98) * mm, "construction": true});
            skLineSegment(sketch, "E560.bottom", {"start": v(-70.97, 73.23) * mm, "end": v(70.95, 73.23) * mm, "construction": true});
            skLineSegment(sketch, "E560.top", {"start": v(-70.97, -68.69) * mm, "end": v(70.95, -68.69) * mm, "construction": true});
            skLineSegment(sketch, "E560.left", {"start": v(-70.97, 73.23) * mm, "end": v(-70.97, -68.69) * mm, "construction": true});
            skLineSegment(sketch, "E560.right", {"start": v(70.95, 73.23) * mm, "end": v(70.95, -68.69) * mm, "construction": true});
            skCircle(sketch, "E561", {"center": v(70.95, 73.23) * mm, "radius": 8 * mm, "construction": true});
            skCircle(sketch, "E562", {"center": v(70.95, -68.69) * mm, "radius": 8 * mm, "construction": true});
            skCircle(sketch, "E563", {"center": v(-70.97, -68.69) * mm, "radius": 8 * mm, "construction": true});
            skCircle(sketch, "E564", {"center": v(-70.97, 73.23) * mm, "radius": 8 * mm, "construction": true});
            skCircle(sketch, "E565", {"center": v(70.95, 73.23) * mm, "radius": 9.5 * mm, "construction": true});
            skCircle(sketch, "E566", {"center": v(70.95, -68.69) * mm, "radius": 9.5 * mm, "construction": true});
            skCircle(sketch, "E567", {"center": v(-70.97, -68.69) * mm, "radius": 9.5 * mm, "construction": true});
            skCircle(sketch, "E568", {"center": v(-70.97, 73.23) * mm, "radius": 9.5 * mm, "construction": true});
            skCircle(sketch, "E569", {"center": v(70.95, 73.23) * mm, "radius": 14 * mm, "construction": true});
            skCircle(sketch, "E570", {"center": v(-70.97, 73.23) * mm, "radius": 14 * mm, "construction": true});
            skCircle(sketch, "E571", {"center": v(70.95, -68.69) * mm, "radius": 14 * mm, "construction": true});
            skCircle(sketch, "E572", {"center": v(-70.97, -68.69) * mm, "radius": 14 * mm, "construction": true});
            skCircle(sketch, "E573", {"center": v(70.95, 73.23) * mm, "radius": 63.5 * mm, "construction": true});
            skCircle(sketch, "E574", {"center": v(70.95, -68.69) * mm, "radius": 63.5 * mm, "construction": true});
            skCircle(sketch, "E575", {"center": v(-70.97, -68.69) * mm, "radius": 63.5 * mm, "construction": true});
            skCircle(sketch, "E576", {"center": v(-70.97, 73.23) * mm, "radius": 63.5 * mm, "construction": true});
            skLineSegment(sketch, "E577", {"start": v(-0.01, 32.52) * mm, "end": v(-0.01, 40.03) * mm, "construction": true});
            skLineSegment(sketch, "E578", {"start": v(-0.01, -27.98) * mm, "end": v(-0.01, -35.48) * mm, "construction": true});
            skLineSegment(sketch, "E579.bottom", {"start": v(-26.18, 28.53) * mm, "end": v(26.2, 28.53) * mm, "construction": true});
            skLineSegment(sketch, "E579.top", {"start": v(-26.22, -23.98) * mm, "end": v(26.16, -23.98) * mm, "construction": true});
            skLineSegment(sketch, "E579.left", {"start": v(-26.18, 28.53) * mm, "end": v(-26.18, -23.85) * mm, "construction": true});
            skLineSegment(sketch, "E579.right", {"start": v(26.2, 28.53) * mm, "end": v(26.2, -23.92) * mm, "construction": true});
            skCircle(sketch, "E580", {"center": v(30.24, 32.52) * mm, "radius": 5 * mm, "construction": true});
            skCircle(sketch, "E581", {"center": v(-30.26, 32.52) * mm, "radius": 5 * mm, "construction": true});
            skCircle(sketch, "E582", {"center": v(30.24, -27.98) * mm, "radius": 5 * mm, "construction": true});
            skCircle(sketch, "E583", {"center": v(-30.26, -27.98) * mm, "radius": 5 * mm, "construction": true});
            skLineSegment(sketch, "E584.bottom", {"start": v(24.49, 26.77) * mm, "end": v(-24.51, 26.77) * mm, "construction": true});
            skLineSegment(sketch, "E584.top", {"start": v(24.49, -22.23) * mm, "end": v(-24.51, -22.23) * mm, "construction": true});
            skLineSegment(sketch, "E584.left", {"start": v(24.49, 26.77) * mm, "end": v(24.49, -22.23) * mm, "construction": true});
            skLineSegment(sketch, "E584.right", {"start": v(-24.51, 26.77) * mm, "end": v(-24.51, -22.23) * mm, "construction": true});
            skLineSegment(sketch, "E585", {"start": v(-26.18, 28.53) * mm, "end": v(-30.26, 32.52) * mm, "construction": true});
            skLineSegment(sketch, "E586", {"start": v(-26.7, 29.02) * mm, "end": v(-33.83, 36.02) * mm, "construction": true});
            skLineSegment(sketch, "E587", {"start": v(-31.82, 34.05) * mm, "end": v(-28.67, 37.26) * mm, "construction": true});
            skLineSegment(sketch, "E588", {"start": v(-31.82, 34.05) * mm, "end": v(-34.97, 30.83) * mm, "construction": true});
            skArc(sketch, "E589", {"start": v(-28.67, 37.26) * mm, "mid": v(-33.83, 36.02) * mm, "end": v(-34.97, 30.83) * mm});
            skLineSegment(sketch, "E590", {"start": v(26.2, 28.53) * mm, "end": v(30.24, 32.52) * mm, "construction": true});
            skLineSegment(sketch, "E591", {"start": v(26.68, 29) * mm, "end": v(33.8, 36.04) * mm, "construction": true});
            skLineSegment(sketch, "E592", {"start": v(31.79, 34.06) * mm, "end": v(34.95, 30.86) * mm, "construction": true});
            skLineSegment(sketch, "E593", {"start": v(31.79, 34.06) * mm, "end": v(28.62, 37.26) * mm, "construction": true});
            skArc(sketch, "E594", {"start": v(34.95, 30.86) * mm, "mid": v(33.8, 36.04) * mm, "end": v(28.62, 37.26) * mm});
            skLineSegment(sketch, "E595", {"start": v(26.16, -23.98) * mm, "end": v(30.24, -27.98) * mm, "construction": true});
            skLineSegment(sketch, "E596", {"start": v(26.67, -24.48) * mm, "end": v(33.8, -31.48) * mm, "construction": true});
            skLineSegment(sketch, "E597", {"start": v(31.8, -29.5) * mm, "end": v(34.94, -26.29) * mm, "construction": true});
            skLineSegment(sketch, "E598", {"start": v(31.8, -29.5) * mm, "end": v(28.64, -32.72) * mm, "construction": true});
            skArc(sketch, "E599", {"start": v(28.64, -32.72) * mm, "mid": v(33.8, -31.48) * mm, "end": v(34.94, -26.29) * mm});
            skLineSegment(sketch, "E600", {"start": v(-26.22, -23.98) * mm, "end": v(-30.26, -27.98) * mm, "construction": true});
            skLineSegment(sketch, "E601", {"start": v(-26.7, -24.46) * mm, "end": v(-33.82, -31.5) * mm, "construction": true});
            skLineSegment(sketch, "E602", {"start": v(-31.81, -29.5) * mm, "end": v(-28.65, -32.7) * mm, "construction": true});
            skLineSegment(sketch, "E603", {"start": v(-31.81, -29.5) * mm, "end": v(-34.98, -26.31) * mm, "construction": true});
            skArc(sketch, "E604", {"start": v(-34.98, -26.31) * mm, "mid": v(-33.82, -31.5) * mm, "end": v(-28.65, -32.7) * mm});
            skLineSegment(sketch, "E605", {"start": v(-34.98, -26.31) * mm, "end": v(-28.29, -8.04) * mm});
            skLineSegment(sketch, "E606", {"start": v(-28.29, 12.59) * mm, "end": v(-34.97, 30.83) * mm});
            skLineSegment(sketch, "E607", {"start": v(34.95, 30.86) * mm, "end": v(28.26, 12.59) * mm});
            skLineSegment(sketch, "E608", {"start": v(28.26, -8.04) * mm, "end": v(34.94, -26.29) * mm});
            skPoint(sketch, "E609.visualSharp", {"position": v(24.49, 2.27) * mm});
            skArc(sketch, "E609.filletArc", {"start": v(28.26, 12.59) * mm, "mid": v(26.43, 2.27) * mm, "end": v(28.26, -8.04) * mm});
            skPoint(sketch, "E610.visualSharp", {"position": v(-24.51, 2.27) * mm});
            skArc(sketch, "E610.filletArc", {"start": v(-28.29, -8.04) * mm, "mid": v(-26.46, 2.27) * mm, "end": v(-28.29, 12.59) * mm});
            skLineSegment(sketch, "E611", {"start": v(-15.28, 22) * mm, "end": v(15.22, 22) * mm, "construction": true});
            skPoint(sketch, "E612.endSnap0", {"position": v(0, -12.98) * mm});
            skLineSegment(sketch, "E613", {"start": v(-15.25, -17.43) * mm, "end": v(15.25, -17.43) * mm, "construction": true});
            skLineSegment(sketch, "E614", {"start": v(-14.34, -35.48) * mm, "end": v(14.32, -35.48) * mm, "construction": true});
            skCircle(sketch, "E615", {"center": v(-30.26, 32.52) * mm, "radius": 1.5 * mm});
            skCircle(sketch, "E616", {"center": v(30.24, 32.52) * mm, "radius": 1.5 * mm});
            skCircle(sketch, "E617", {"center": v(15.22, 17.52) * mm, "radius": 1.5 * mm});
            skCircle(sketch, "E618", {"center": v(-15.28, 17.52) * mm, "radius": 1.5 * mm});
            skCircle(sketch, "E619", {"center": v(-15.25, -12.98) * mm, "radius": 1.5 * mm});
            skCircle(sketch, "E620", {"center": v(15.25, -12.98) * mm, "radius": 1.5 * mm});
            skCircle(sketch, "E621", {"center": v(30.24, -27.98) * mm, "radius": 1.5 * mm});
            skCircle(sketch, "E622", {"center": v(-30.26, -27.98) * mm, "radius": 1.5 * mm});
            skLineSegment(sketch, "E623", {"start": v(14.32, 40.03) * mm, "end": v(10.32, 40.03) * mm, "construction": true});
            skLineSegment(sketch, "E624", {"start": v(-14.34, 40.03) * mm, "end": v(-10.34, 40.03) * mm, "construction": true});
            skLineSegment(sketch, "E625", {"start": v(10.32, 40.03) * mm, "end": v(10.32, 36.03) * mm, "construction": true});
            skLineSegment(sketch, "E626", {"start": v(-10.34, 40.03) * mm, "end": v(-10.34, 36.03) * mm, "construction": true});
            skLineSegment(sketch, "E627", {"start": v(-0.01, 40.03) * mm, "end": v(-0.03, 17.52) * mm, "construction": true});
            skPoint(sketch, "E628.visualSharp", {"position": v(-14.34, -35.48) * mm});
            skPoint(sketch, "E629.visualSharp", {"position": v(14.32, -35.48) * mm});
            skCircle(sketch, "E630", {"center": v(-0.01, 2.27) * mm, "radius": 17.1 * mm, "construction": true});
            skLineSegment(sketch, "E631", {"start": v(-0.01, 2.27) * mm, "end": v(14.08, 16.37) * mm, "construction": true});
            skLineSegment(sketch, "E632", {"start": v(-0.01, 2.27) * mm, "end": v(-15.28, 17.52) * mm, "construction": true});
            skLineSegment(sketch, "E633", {"start": v(-0.01, 2.27) * mm, "end": v(-15.32, -13.05) * mm, "construction": true});
            skLineSegment(sketch, "E634", {"start": v(-0.01, 2.27) * mm, "end": v(15.25, -12.98) * mm, "construction": true});
            skLineSegment(sketch, "E635", {"start": v(-10.71, 12.96) * mm, "end": v(-7.89, 15.8) * mm, "construction": true});
            skLineSegment(sketch, "E636", {"start": v(-10.71, 12.96) * mm, "end": v(-13.54, 10.13) * mm, "construction": true});
            skLineSegment(sketch, "E637", {"start": v(9.01, 11.3) * mm, "end": v(11.84, 8.47) * mm, "construction": true});
            skLineSegment(sketch, "E638", {"start": v(9.01, 11.3) * mm, "end": v(6.19, 14.13) * mm, "construction": true});
            skLineSegment(sketch, "E639", {"start": v(9.8, -7.53) * mm, "end": v(12.63, -4.7) * mm, "construction": true});
            skLineSegment(sketch, "E640", {"start": v(9.8, -7.53) * mm, "end": v(6.97, -10.36) * mm, "construction": true});
            skLineSegment(sketch, "E641", {"start": v(-9.52, -7.25) * mm, "end": v(-6.7, -10.07) * mm, "construction": true});
            skLineSegment(sketch, "E642", {"start": v(-9.52, -7.25) * mm, "end": v(-12.35, -4.42) * mm, "construction": true});
            skLineSegment(sketch, "E643.bottom", {"start": v(6.34, 8.62) * mm, "end": v(-6.36, 8.62) * mm, "construction": true});
            skLineSegment(sketch, "E643.top", {"start": v(6.34, -4.08) * mm, "end": v(-6.36, -4.08) * mm, "construction": true});
            skLineSegment(sketch, "E643.left", {"start": v(6.34, 8.62) * mm, "end": v(6.34, -4.08) * mm, "construction": true});
            skLineSegment(sketch, "E643.right", {"start": v(-6.36, 8.62) * mm, "end": v(-6.36, -4.08) * mm, "construction": true});
            skLineSegment(sketch, "E644", {"start": v(6.19, 14.13) * mm, "end": v(8.92, 16.86) * mm, "construction": true});
            skLineSegment(sketch, "E645", {"start": v(11.84, 8.47) * mm, "end": v(14.57, 11.2) * mm, "construction": true});
            skLineSegment(sketch, "E646", {"start": v(7.98, 15.92) * mm, "end": v(1.4, 9.34) * mm});
            skLineSegment(sketch, "E647", {"start": v(-1.43, 9.34) * mm, "end": v(-8, 15.92) * mm});
            skLineSegment(sketch, "E648", {"start": v(-13.54, 10.13) * mm, "end": v(-14.6, 11.2) * mm, "construction": true});
            skLineSegment(sketch, "E649", {"start": v(-6.7, -10.07) * mm, "end": v(-8.93, -12.32) * mm, "construction": true});
            skLineSegment(sketch, "E650", {"start": v(-8, -11.38) * mm, "end": v(-1.43, -4.8) * mm});
            skLineSegment(sketch, "E651", {"start": v(1.4, -4.8) * mm, "end": v(7.98, -11.37) * mm});
            skLineSegment(sketch, "E652", {"start": v(13.64, 10.27) * mm, "end": v(7.06, 3.69) * mm});
            skLineSegment(sketch, "E653", {"start": v(7.06, 0.86) * mm, "end": v(13.64, -5.72) * mm});
            skPoint(sketch, "E654", {"position": v(-7.75, 17.52) * mm});
            skPoint(sketch, "E655", {"position": v(7.72, 17.52) * mm});
            skPoint(sketch, "E656", {"position": v(15.22, 10.04) * mm});
            skPoint(sketch, "E657", {"position": v(15.22, -5.5) * mm});
            skPoint(sketch, "E658", {"position": v(7.72, -12.98) * mm});
            skPoint(sketch, "E659", {"position": v(-7.75, -12.98) * mm});
            skPoint(sketch, "E660", {"position": v(-15.25, -5.5) * mm});
            skPoint(sketch, "E661", {"position": v(-15.25, 10.04) * mm});
            skLineSegment(sketch, "E662", {"start": v(-7.79, 17.5) * mm, "end": v(-7.75, 17.52) * mm});
            skLineSegment(sketch, "E663", {"start": v(7.76, 17.5) * mm, "end": v(7.72, 17.52) * mm});
            skLineSegment(sketch, "E664", {"start": v(15.22, 10.05) * mm, "end": v(15.22, 10.04) * mm});
            skLineSegment(sketch, "E665", {"start": v(15.22, -5.5) * mm, "end": v(15.22, -5.5) * mm});
            skLineSegment(sketch, "E666", {"start": v(7.76, -12.96) * mm, "end": v(7.72, -12.98) * mm});
            skLineSegment(sketch, "E667", {"start": v(-7.75, -12.98) * mm, "end": v(-7.78, -12.96) * mm});
            skLineSegment(sketch, "E668", {"start": v(-15.24, -5.5) * mm, "end": v(-15.25, -5.5) * mm});
            skLineSegment(sketch, "E669", {"start": v(-15.24, 10.05) * mm, "end": v(-15.25, 10.04) * mm});
            skPoint(sketch, "E670", {"position": v(-0.03, 19.37) * mm});
            skPoint(sketch, "E671", {"position": v(17.09, 2.27) * mm});
            skPoint(sketch, "E672", {"position": v(-17.11, 2.27) * mm});
            skPoint(sketch, "E673", {"position": v(-0.01, -14.83) * mm});
            skArc(sketch, "E674", {"start": v(15.22, -5.5) * mm, "mid": v(17.09, 2.27) * mm, "end": v(15.22, 10.04) * mm});
            skArc(sketch, "E675", {"start": v(-15.25, 10.04) * mm, "mid": v(-17.11, 2.27) * mm, "end": v(-15.25, -5.5) * mm});
            skPoint(sketch, "E676.visualSharp", {"position": v(-5.66, 2.27) * mm});
            skPoint(sketch, "E677.visualSharp", {"position": v(-14.6, 11.2) * mm});
            skArc(sketch, "E677.filletArc", {"start": v(-13.66, 10.27) * mm, "mid": v(-14.5, 10.55) * mm, "end": v(-15.24, 10.05) * mm});
            skPoint(sketch, "E678.visualSharp", {"position": v(-14.6, -6.66) * mm});
            skArc(sketch, "E678.filletArc", {"start": v(-15.24, -5.5) * mm, "mid": v(-14.5, -6.01) * mm, "end": v(-13.66, -5.73) * mm});
            skPoint(sketch, "E679.visualSharp", {"position": v(-8.94, 16.86) * mm});
            skArc(sketch, "E679.filletArc", {"start": v(-7.79, 17.5) * mm, "mid": v(-8.3, 16.77) * mm, "end": v(-8, 15.92) * mm});
            skPoint(sketch, "E680.visualSharp", {"position": v(8.92, 16.86) * mm});
            skArc(sketch, "E680.filletArc", {"start": v(7.98, 15.92) * mm, "mid": v(8.26, 16.77) * mm, "end": v(7.76, 17.5) * mm});
            skPoint(sketch, "E681.visualSharp", {"position": v(14.57, -6.66) * mm});
            skArc(sketch, "E681.filletArc", {"start": v(13.64, -5.72) * mm, "mid": v(14.48, -6) * mm, "end": v(15.22, -5.5) * mm});
            skPoint(sketch, "E682.visualSharp", {"position": v(14.57, 11.2) * mm});
            skArc(sketch, "E682.filletArc", {"start": v(15.22, 10.05) * mm, "mid": v(14.48, 10.55) * mm, "end": v(13.64, 10.27) * mm});
            skPoint(sketch, "E683.visualSharp", {"position": v(8.92, -12.3) * mm});
            skArc(sketch, "E683.filletArc", {"start": v(7.76, -12.96) * mm, "mid": v(8.27, -12.22) * mm, "end": v(7.98, -11.37) * mm});
            skPoint(sketch, "E684.visualSharp", {"position": v(-8.93, -12.32) * mm});
            skArc(sketch, "E684.filletArc", {"start": v(-8, -11.38) * mm, "mid": v(-8.28, -12.23) * mm, "end": v(-7.78, -12.96) * mm});
            skLineSegment(sketch, "E685", {"start": v(-13.66, 10.27) * mm, "end": v(-7.08, 3.68) * mm});
            skLineSegment(sketch, "E686", {"start": v(-13.66, -5.73) * mm, "end": v(-7.08, 0.86) * mm});
            skArc(sketch, "E687.filletArc", {"start": v(-7.08, 0.86) * mm, "mid": v(-6.5, 2.27) * mm, "end": v(-7.08, 3.68) * mm});
            skPoint(sketch, "E688.visualSharp", {"position": v(-0.01, -3.39) * mm});
            skArc(sketch, "E688.filletArc", {"start": v(1.4, -4.8) * mm, "mid": v(-0.01, -4.22) * mm, "end": v(-1.43, -4.8) * mm});
            skPoint(sketch, "E689.visualSharp", {"position": v(5.64, 2.27) * mm});
            skArc(sketch, "E689.filletArc", {"start": v(7.06, 3.69) * mm, "mid": v(6.47, 2.27) * mm, "end": v(7.06, 0.86) * mm});
            skPoint(sketch, "E690.visualSharp", {"position": v(-0.02, 7.93) * mm});
            skArc(sketch, "E690.filletArc", {"start": v(-1.43, 9.34) * mm, "mid": v(-0.02, 8.76) * mm, "end": v(1.4, 9.34) * mm});
            skLineSegment(sketch, "E691", {"start": v(-12.93, 15.17) * mm, "end": v(-11.16, 16.94) * mm, "construction": true});
            skLineSegment(sketch, "E692", {"start": v(-12.93, 15.17) * mm, "end": v(-14.7, 13.4) * mm, "construction": true});
            skLineSegment(sketch, "E693", {"start": v(-14.7, 13.4) * mm, "end": v(-27.43, 26.13) * mm, "construction": true});
            skPoint(sketch, "E694", {"position": v(-17.59, 16.3) * mm});
            skCircle(sketch, "E695", {"center": v(-15.28, 17.52) * mm, "radius": 4.62 * mm, "construction": true});
            skLineSegment(sketch, "E696", {"start": v(-27.43, 26.13) * mm, "end": v(-21.13, 10.9) * mm, "construction": true});
            skLineSegment(sketch, "E697", {"start": v(-15.28, 17.52) * mm, "end": v(-21.35, 11.45) * mm, "construction": true});
            skLineSegment(sketch, "E698", {"start": v(-18.88, 13.92) * mm, "end": v(-19.76, 13.03) * mm});
            skLineSegment(sketch, "E699", {"start": v(-22.2, 13.52) * mm, "end": v(-25.5, 21.5) * mm});
            skLineSegment(sketch, "E700", {"start": v(-23.88, 22.58) * mm, "end": v(-20.07, 18.78) * mm});
            skLineSegment(sketch, "E701", {"start": v(-19.86, 18.13) * mm, "end": v(-19.88, 18.01) * mm});
            skLineSegment(sketch, "E702", {"start": v(-18.86, 14.6) * mm, "end": v(-18.88, 14.62) * mm});
            skPoint(sketch, "E703", {"position": v(-19.7, 16.17) * mm});
            skArc(sketch, "E704", {"start": v(-19.88, 18.01) * mm, "mid": v(-19.72, 16.22) * mm, "end": v(-18.88, 14.62) * mm});
            skPoint(sketch, "E705.visualSharp", {"position": v(-27.43, 26.13) * mm});
            skArc(sketch, "E705.filletArc", {"start": v(-23.88, 22.58) * mm, "mid": v(-25.14, 22.7) * mm, "end": v(-25.5, 21.5) * mm});
            skPoint(sketch, "E706.visualSharp", {"position": v(-21.35, 11.45) * mm});
            skArc(sketch, "E706.filletArc", {"start": v(-22.2, 13.52) * mm, "mid": v(-21.12, 12.62) * mm, "end": v(-19.76, 13.03) * mm});
            skPoint(sketch, "E707.visualSharp", {"position": v(-18.55, 14.25) * mm});
            skArc(sketch, "E707.filletArc", {"start": v(-18.88, 13.92) * mm, "mid": v(-18.74, 14.26) * mm, "end": v(-18.86, 14.6) * mm});
            skPoint(sketch, "E708.visualSharp", {"position": v(-19.8, 18.5) * mm});
            skArc(sketch, "E708.filletArc", {"start": v(-19.86, 18.13) * mm, "mid": v(-19.89, 18.48) * mm, "end": v(-20.07, 18.78) * mm});
            skCircle(sketch, "E709", {"center": v(15.22, 17.54) * mm, "radius": 4.62 * mm, "construction": true});
            skLineSegment(sketch, "E710", {"start": v(15.22, 17.54) * mm, "end": v(12.89, 15.18) * mm, "construction": true});
            skLineSegment(sketch, "E711", {"start": v(12.89, 15.18) * mm, "end": v(14.67, 13.42) * mm, "construction": true});
            skLineSegment(sketch, "E712", {"start": v(12.89, 15.18) * mm, "end": v(11.1, 16.93) * mm, "construction": true});
            skLineSegment(sketch, "E713", {"start": v(11.1, 16.93) * mm, "end": v(23.84, 29.66) * mm, "construction": true});
            skLineSegment(sketch, "E714", {"start": v(14.67, 13.42) * mm, "end": v(27.3, 26.24) * mm, "construction": true});
            skLineSegment(sketch, "E715", {"start": v(15.22, 17.52) * mm, "end": v(21.34, 11.5) * mm, "construction": true});
            skLineSegment(sketch, "E716", {"start": v(21.34, 11.5) * mm, "end": v(27.3, 26.24) * mm, "construction": true});
            skLineSegment(sketch, "E717", {"start": v(19.8, 18.17) * mm, "end": v(19.81, 18.06) * mm});
            skLineSegment(sketch, "E718", {"start": v(18.82, 14.64) * mm, "end": v(18.84, 14.66) * mm});
            skLineSegment(sketch, "E719", {"start": v(20, 18.83) * mm, "end": v(23.79, 22.67) * mm});
            skLineSegment(sketch, "E720", {"start": v(25.43, 21.6) * mm, "end": v(22.18, 13.58) * mm});
            skLineSegment(sketch, "E721", {"start": v(19.74, 13.07) * mm, "end": v(18.84, 13.95) * mm});
            skPoint(sketch, "E722", {"position": v(19.64, 16.2) * mm});
            skArc(sketch, "E723", {"start": v(18.84, 14.66) * mm, "mid": v(19.66, 16.26) * mm, "end": v(19.81, 18.06) * mm});
            skPoint(sketch, "E724.visualSharp", {"position": v(18.5, 14.29) * mm});
            skArc(sketch, "E724.filletArc", {"start": v(18.82, 14.64) * mm, "mid": v(18.7, 14.3) * mm, "end": v(18.84, 13.95) * mm});
            skPoint(sketch, "E725.visualSharp", {"position": v(19.73, 18.55) * mm});
            skArc(sketch, "E725.filletArc", {"start": v(20, 18.83) * mm, "mid": v(19.82, 18.52) * mm, "end": v(19.8, 18.17) * mm});
            skPoint(sketch, "E726.visualSharp", {"position": v(27.3, 26.24) * mm});
            skArc(sketch, "E726.filletArc", {"start": v(25.43, 21.6) * mm, "mid": v(25.05, 22.8) * mm, "end": v(23.79, 22.67) * mm});
            skPoint(sketch, "E727.visualSharp", {"position": v(21.34, 11.5) * mm});
            skArc(sketch, "E727.filletArc", {"start": v(19.74, 13.07) * mm, "mid": v(21.1, 12.67) * mm, "end": v(22.18, 13.58) * mm});
            skCircle(sketch, "E728", {"center": v(-15.25, -12.98) * mm, "radius": 4.62 * mm, "construction": true});
            skCircle(sketch, "E729", {"center": v(15.25, -12.98) * mm, "radius": 4.62 * mm, "construction": true});
            skLineSegment(sketch, "E730", {"start": v(-15.25, -12.98) * mm, "end": v(-12.9, -10.63) * mm, "construction": true});
            skLineSegment(sketch, "E731", {"start": v(-12.9, -10.63) * mm, "end": v(-11.14, -12.4) * mm, "construction": true});
            skLineSegment(sketch, "E732", {"start": v(-12.9, -10.63) * mm, "end": v(-14.67, -8.87) * mm, "construction": true});
            skLineSegment(sketch, "E733", {"start": v(-11.14, -12.4) * mm, "end": v(-23.86, -25.13) * mm, "construction": true});
            skLineSegment(sketch, "E734", {"start": v(-14.67, -8.87) * mm, "end": v(-27.4, -21.6) * mm, "construction": true});
            skLineSegment(sketch, "E735", {"start": v(-15.25, -12.98) * mm, "end": v(-9.17, -19.05) * mm, "construction": true});
            skLineSegment(sketch, "E736", {"start": v(-15.25, -12.98) * mm, "end": v(-21.32, -6.9) * mm, "construction": true});
            skLineSegment(sketch, "E737", {"start": v(-25.48, -16.95) * mm, "end": v(-22.18, -8.98) * mm});
            skLineSegment(sketch, "E738", {"start": v(-19.73, -8.5) * mm, "end": v(-18.85, -9.37) * mm});
            skLineSegment(sketch, "E739", {"start": v(-23.85, -18.04) * mm, "end": v(-20.04, -14.23) * mm});
            skLineSegment(sketch, "E740", {"start": v(-18.83, -10.06) * mm, "end": v(-18.85, -10.08) * mm});
            skLineSegment(sketch, "E741", {"start": v(-19.83, -13.58) * mm, "end": v(-19.85, -13.47) * mm});
            skPoint(sketch, "E742", {"position": v(-19.68, -11.67) * mm});
            skArc(sketch, "E743", {"start": v(-18.85, -10.08) * mm, "mid": v(-19.68, -11.67) * mm, "end": v(-19.85, -13.47) * mm});
            skPoint(sketch, "E744.visualSharp", {"position": v(-18.52, -9.7) * mm});
            skArc(sketch, "E744.filletArc", {"start": v(-18.83, -10.06) * mm, "mid": v(-18.7, -9.71) * mm, "end": v(-18.85, -9.37) * mm});
            skPoint(sketch, "E745.visualSharp", {"position": v(-19.77, -13.96) * mm});
            skArc(sketch, "E745.filletArc", {"start": v(-20.04, -14.23) * mm, "mid": v(-19.85, -13.93) * mm, "end": v(-19.83, -13.58) * mm});
            skPoint(sketch, "E746.visualSharp", {"position": v(-27.4, -21.6) * mm});
            skArc(sketch, "E746.filletArc", {"start": v(-25.48, -16.95) * mm, "mid": v(-25.11, -18.17) * mm, "end": v(-23.85, -18.04) * mm});
            skPoint(sketch, "E747.visualSharp", {"position": v(-21.32, -6.9) * mm});
            skArc(sketch, "E747.filletArc", {"start": v(-19.73, -8.5) * mm, "mid": v(-21.09, -8.08) * mm, "end": v(-22.18, -8.98) * mm});
            skLineSegment(sketch, "E748", {"start": v(15.25, -12.98) * mm, "end": v(12.9, -10.63) * mm, "construction": true});
            skLineSegment(sketch, "E749", {"start": v(12.9, -10.63) * mm, "end": v(14.68, -8.87) * mm, "construction": true});
            skLineSegment(sketch, "E750", {"start": v(12.9, -10.63) * mm, "end": v(11.14, -12.4) * mm, "construction": true});
            skLineSegment(sketch, "E751", {"start": v(14.68, -8.87) * mm, "end": v(27.4, -21.59) * mm, "construction": true});
            skLineSegment(sketch, "E752", {"start": v(15.25, -12.98) * mm, "end": v(21.32, -6.9) * mm, "construction": true});
            skLineSegment(sketch, "E753", {"start": v(22.18, -8.97) * mm, "end": v(25.49, -16.95) * mm});
            skLineSegment(sketch, "E754", {"start": v(23.86, -18.04) * mm, "end": v(20.04, -14.23) * mm});
            skLineSegment(sketch, "E755", {"start": v(19.74, -8.49) * mm, "end": v(18.86, -9.37) * mm});
            skLineSegment(sketch, "E756", {"start": v(18.84, -10.06) * mm, "end": v(18.86, -10.08) * mm});
            skLineSegment(sketch, "E757", {"start": v(19.83, -13.58) * mm, "end": v(19.85, -13.46) * mm});
            skPoint(sketch, "E758", {"position": v(19.64, -11.53) * mm});
            skArc(sketch, "E759", {"start": v(19.85, -13.46) * mm, "mid": v(19.69, -11.67) * mm, "end": v(18.86, -10.08) * mm});
            skPoint(sketch, "E760.visualSharp", {"position": v(21.32, -6.9) * mm});
            skArc(sketch, "E760.filletArc", {"start": v(22.18, -8.97) * mm, "mid": v(21.1, -8.08) * mm, "end": v(19.74, -8.49) * mm});
            skPoint(sketch, "E761.visualSharp", {"position": v(19.77, -13.96) * mm});
            skArc(sketch, "E761.filletArc", {"start": v(19.83, -13.58) * mm, "mid": v(19.86, -13.93) * mm, "end": v(20.04, -14.23) * mm});
            skPoint(sketch, "E762.visualSharp", {"position": v(18.52, -9.7) * mm});
            skArc(sketch, "E762.filletArc", {"start": v(18.86, -9.37) * mm, "mid": v(18.71, -9.7) * mm, "end": v(18.84, -10.06) * mm});
            skPoint(sketch, "E763.visualSharp", {"position": v(27.4, -21.59) * mm});
            skArc(sketch, "E763.filletArc", {"start": v(23.86, -18.04) * mm, "mid": v(25.12, -18.16) * mm, "end": v(25.49, -16.95) * mm});
            skLineSegment(sketch, "E764", {"start": v(-0.01, -29.14) * mm, "end": v(15.24, -29.14) * mm, "construction": true});
            skPoint(sketch, "E765.visualSharp", {"position": v(-9.17, -19.05) * mm});
            skPoint(sketch, "E766.visualSharp", {"position": v(-11.98, -16.25) * mm});
            skPoint(sketch, "E767.visualSharp", {"position": v(-16.23, -17.5) * mm});
            skPoint(sketch, "E768.visualSharp", {"position": v(-23.86, -25.13) * mm});
            skLineSegment(sketch, "E769", {"start": v(15.25, -12.98) * mm, "end": v(9.18, -19.05) * mm, "construction": true});
            skLineSegment(sketch, "E770", {"start": v(11.14, -12.4) * mm, "end": v(23.88, -25.12) * mm, "construction": true});
            skPoint(sketch, "E771", {"position": v(13.76, -17.36) * mm});
            skPoint(sketch, "E772.visualSharp", {"position": v(9.18, -19.05) * mm});
            skPoint(sketch, "E773.visualSharp", {"position": v(11.98, -16.25) * mm});
            skPoint(sketch, "E774.visualSharp", {"position": v(23.88, -25.12) * mm});
            skPoint(sketch, "E775.visualSharp", {"position": v(16.24, -17.5) * mm});
            skPoint(sketch, "E776", {"position": v(-14.29, -17.5) * mm});
            skLineSegment(sketch, "E777", {"start": v(-28.67, 37.26) * mm, "end": v(-26.94, 36.26) * mm, "construction": true});
            skLineSegment(sketch, "E778", {"start": v(28.62, 37.26) * mm, "end": v(26.9, 36.24) * mm, "construction": true});
            skPoint(sketch, "E779", {"position": v(27.69, 36.82) * mm});
            skArc(sketch, "E780", {"start": v(28.62, 37.26) * mm, "mid": v(27.7, 36.84) * mm, "end": v(26.9, 36.24) * mm});
            skPoint(sketch, "E781", {"position": v(-27.73, 36.83) * mm});
            skArc(sketch, "E782", {"start": v(-26.94, 36.26) * mm, "mid": v(-27.76, 36.85) * mm, "end": v(-28.67, 37.26) * mm});
            skLineSegment(sketch, "E783", {"start": v(-26.94, 36.26) * mm, "end": v(-15.28, 26.77) * mm});
            skLineSegment(sketch, "E784", {"start": v(26.9, 36.24) * mm, "end": v(15.22, 26.77) * mm});
            skPoint(sketch, "E785", {"position": v(-0.03, 22) * mm});
            skFitSpline(sketch, "E786", {"points": [v(-15.28, 26.77) * mm, v(-0.03, 22) * mm, v(15.22, 26.77) * mm], "startDerivative": vector(26.4, -17.68) * mm, "endDerivative": vector(26.05, 17.77) * mm});
            skLineSegment(sketch, "E787", {"start": v(10.88, 23.81) * mm, "end": v(0, 23.82) * mm, "construction": true});
            skLineSegment(sketch, "E788", {"start": v(0, 23.82) * mm, "end": v(-10.88, 23.83) * mm, "construction": true});
            skLineSegment(sketch, "E789", {"start": v(-28.65, -32.7) * mm, "end": v(-26.92, -31.7) * mm, "construction": true});
            skLineSegment(sketch, "E790", {"start": v(28.64, -32.72) * mm, "end": v(26.91, -31.71) * mm, "construction": true});
            skPoint(sketch, "E791", {"position": v(27.67, -32.27) * mm});
            skArc(sketch, "E792", {"start": v(26.91, -31.71) * mm, "mid": v(27.73, -32.3) * mm, "end": v(28.64, -32.72) * mm});
            skPoint(sketch, "E793", {"position": v(-27.7, -32.27) * mm});
            skArc(sketch, "E794", {"start": v(-28.65, -32.7) * mm, "mid": v(-27.73, -32.29) * mm, "end": v(-26.92, -31.7) * mm});
            skLineSegment(sketch, "E795", {"start": v(-0.01, -29.14) * mm, "end": v(-15.26, -29.14) * mm, "construction": true});
            skLineSegment(sketch, "E796", {"start": v(-26.92, -31.7) * mm, "end": v(-15.26, -23.98) * mm});
            skLineSegment(sketch, "E797", {"start": v(26.91, -31.71) * mm, "end": v(15.24, -23.98) * mm});
            skLineSegment(sketch, "E798", {"start": v(-0.01, -14.83) * mm, "end": v(-0.01, -17.45) * mm, "construction": true});
            skLineSegment(sketch, "E799", {"start": v(-0.01, -17.45) * mm, "end": v(-0.01, -19.27) * mm, "construction": true});
            skFitSpline(sketch, "E800", {"points": [v(-15.26, -23.98) * mm, v(-0.01, -17.45) * mm, v(15.24, -23.98) * mm], "startDerivative": vector(30.5, 19.6) * mm, "endDerivative": vector(30.5, -19.6) * mm});
            skLineSegment(sketch, "E801", {"start": v(-0.01, -19.27) * mm, "end": v(10.87, -19.27) * mm, "construction": true});
            skLineSegment(sketch, "E802", {"start": v(-0.01, -19.27) * mm, "end": v(-10.9, -19.27) * mm, "construction": true});
            skLineSegment(sketch, "E803", {"start": v(0, -12.98) * mm, "end": v(0, -10.98) * mm, "construction": true});
            skFitSpline(sketch, "E804", {"points": [v(-7.75, -12.98) * mm, v(0, -10.98) * mm, v(7.72, -12.98) * mm], "startDerivative": vector(15.5, 6) * mm, "endDerivative": vector(15.45, -6) * mm});
            skLineSegment(sketch, "E805", {"start": v(-0.03, 17.52) * mm, "end": v(-0.03, 15.52) * mm, "construction": true});
            skFitSpline(sketch, "E806", {"points": [v(-7.75, 17.52) * mm, v(-0.03, 15.52) * mm, v(7.72, 17.52) * mm], "startDerivative": vector(15.45, -6) * mm, "endDerivative": vector(15.5, 6) * mm});
            skSolve(sketch);
        }
        {
            var Q0;
            Q0=qCreatedBy(makeId("Top.planeOp"),FACE);
            var sketch = newSketch(context, id + "F6", { "sketchPlane" : qUnion([Q0])});
            skLineSegment(sketch, "E807.bottom", {"start": v(-15.25, 15.28) * mm, "end": v(15.25, 15.28) * mm, "construction": true});
            skLineSegment(sketch, "E807.top", {"start": v(-15.25, -15.22) * mm, "end": v(15.25, -15.22) * mm, "construction": true});
            skLineSegment(sketch, "E807.left", {"start": v(-15.25, 15.28) * mm, "end": v(-15.25, -15.22) * mm, "construction": true});
            skLineSegment(sketch, "E807.right", {"start": v(15.25, 15.28) * mm, "end": v(15.25, -15.22) * mm, "construction": true});
            skPoint(sketch, "E807.middle", {"position": v(0, 0.03) * mm});
            skLineSegment(sketch, "E808.bottom", {"start": v(30.25, 30.28) * mm, "end": v(-30.25, 30.28) * mm, "construction": true});
            skLineSegment(sketch, "E808.top", {"start": v(30.25, -30.22) * mm, "end": v(-30.25, -30.22) * mm, "construction": true});
            skLineSegment(sketch, "E808.left", {"start": v(30.25, 30.28) * mm, "end": v(30.25, -30.22) * mm, "construction": true});
            skLineSegment(sketch, "E808.right", {"start": v(-30.25, 30.28) * mm, "end": v(-30.25, -30.22) * mm, "construction": true});
            skLineSegment(sketch, "E809.bottom", {"start": v(-70.96, 70.99) * mm, "end": v(70.96, 70.99) * mm, "construction": true});
            skLineSegment(sketch, "E809.top", {"start": v(-70.96, -70.93) * mm, "end": v(70.96, -70.93) * mm, "construction": true});
            skLineSegment(sketch, "E809.left", {"start": v(-70.96, 70.99) * mm, "end": v(-70.96, -70.93) * mm, "construction": true});
            skLineSegment(sketch, "E809.right", {"start": v(70.96, 70.99) * mm, "end": v(70.96, -70.93) * mm, "construction": true});
            skCircle(sketch, "E810", {"center": v(70.96, 70.99) * mm, "radius": 4.5 * mm, "construction": true});
            skCircle(sketch, "E811", {"center": v(-70.96, 70.99) * mm, "radius": 4.5 * mm, "construction": true});
            skCircle(sketch, "E812", {"center": v(70.96, -70.93) * mm, "radius": 4.5 * mm, "construction": true});
            skCircle(sketch, "E813", {"center": v(-70.96, -70.93) * mm, "radius": 4.5 * mm, "construction": true});
            skCircle(sketch, "E814", {"center": v(70.96, 70.99) * mm, "radius": 8 * mm, "construction": true});
            skCircle(sketch, "E815", {"center": v(70.96, -70.93) * mm, "radius": 8 * mm, "construction": true});
            skCircle(sketch, "E816", {"center": v(-70.96, -70.93) * mm, "radius": 8 * mm, "construction": true});
            skCircle(sketch, "E817", {"center": v(-70.96, 70.99) * mm, "radius": 8 * mm, "construction": true});
            skCircle(sketch, "E818", {"center": v(70.96, 70.99) * mm, "radius": 9.5 * mm, "construction": true});
            skCircle(sketch, "E819", {"center": v(70.96, -70.93) * mm, "radius": 9.5 * mm, "construction": true});
            skCircle(sketch, "E820", {"center": v(-70.96, -70.93) * mm, "radius": 9.5 * mm, "construction": true});
            skCircle(sketch, "E821", {"center": v(-70.96, 70.99) * mm, "radius": 9.5 * mm, "construction": true});
            skCircle(sketch, "E822", {"center": v(70.96, 70.99) * mm, "radius": 14 * mm, "construction": true});
            skCircle(sketch, "E823", {"center": v(-70.96, 70.99) * mm, "radius": 14 * mm, "construction": true});
            skCircle(sketch, "E824", {"center": v(70.96, -70.93) * mm, "radius": 14 * mm, "construction": true});
            skCircle(sketch, "E825", {"center": v(-70.96, -70.93) * mm, "radius": 14 * mm, "construction": true});
            skCircle(sketch, "E826", {"center": v(70.96, 70.99) * mm, "radius": 63.5 * mm, "construction": true});
            skCircle(sketch, "E827", {"center": v(70.96, -70.93) * mm, "radius": 63.5 * mm, "construction": true});
            skCircle(sketch, "E828", {"center": v(-70.96, -70.93) * mm, "radius": 63.5 * mm, "construction": true});
            skCircle(sketch, "E829", {"center": v(-70.96, 70.99) * mm, "radius": 63.5 * mm, "construction": true});
            skLineSegment(sketch, "E830", {"start": v(0, 30.28) * mm, "end": v(0, 33.77) * mm, "construction": true});
            skLineSegment(sketch, "E831", {"start": v(0, 33.77) * mm, "end": v(-15, 33.77) * mm, "construction": true});
            skLineSegment(sketch, "E832", {"start": v(0, 33.77) * mm, "end": v(15, 33.77) * mm, "construction": true});
            skLineSegment(sketch, "E833", {"start": v(0, -30.22) * mm, "end": v(0, -33.72) * mm, "construction": true});
            skLineSegment(sketch, "E834", {"start": v(0, -33.72) * mm, "end": v(-15, -33.72) * mm, "construction": true});
            skLineSegment(sketch, "E835", {"start": v(0, -33.72) * mm, "end": v(15, -33.72) * mm, "construction": true});
            skLineSegment(sketch, "E836.bottom", {"start": v(-26.19, 26.22) * mm, "end": v(26.2, 26.22) * mm, "construction": true});
            skLineSegment(sketch, "E836.top", {"start": v(-26.19, -26.16) * mm, "end": v(26.2, -26.16) * mm, "construction": true});
            skLineSegment(sketch, "E836.left", {"start": v(-26.19, 26.22) * mm, "end": v(-26.19, -26.16) * mm, "construction": true});
            skLineSegment(sketch, "E836.right", {"start": v(26.2, 26.22) * mm, "end": v(26.2, -26.16) * mm, "construction": true});
            skCircle(sketch, "E837", {"center": v(30.25, 30.28) * mm, "radius": 3.57 * mm, "construction": true});
            skCircle(sketch, "E838", {"center": v(-30.25, 30.28) * mm, "radius": 3.57 * mm, "construction": true});
            skCircle(sketch, "E839", {"center": v(30.25, -30.22) * mm, "radius": 3.57 * mm, "construction": true});
            skCircle(sketch, "E840", {"center": v(-30.25, -30.22) * mm, "radius": 3.57 * mm, "construction": true});
            skLineSegment(sketch, "E841", {"start": v(-70.96, 70.99) * mm, "end": v(70.96, -70.93) * mm, "construction": true});
            skLineSegment(sketch, "E842", {"start": v(0, -26.16) * mm, "end": v(17.54, -26.16) * mm, "construction": true});
            skLineSegment(sketch, "E843", {"start": v(0, -26.16) * mm, "end": v(-17.54, -26.16) * mm, "construction": true});
            skLineSegment(sketch, "E844", {"start": v(0, -33.72) * mm, "end": v(0, -44.57) * mm, "construction": true});
            skLineSegment(sketch, "E845", {"start": v(0, -44.57) * mm, "end": v(0, -48.1) * mm, "construction": true});
            skLineSegment(sketch, "E846", {"start": v(0, -44.57) * mm, "end": v(11, -44.57) * mm, "construction": true});
            skLineSegment(sketch, "E847", {"start": v(0, -44.57) * mm, "end": v(-11, -44.57) * mm, "construction": true});
            skLineSegment(sketch, "E848", {"start": v(-15.25, -15.22) * mm, "end": v(-19.25, -15.22) * mm, "construction": true});
            skLineSegment(sketch, "E849", {"start": v(15.25, -15.22) * mm, "end": v(19.25, -15.22) * mm, "construction": true});
            skLineSegment(sketch, "E850", {"start": v(15.25, 15.28) * mm, "end": v(19.25, 15.28) * mm, "construction": true});
            skLineSegment(sketch, "E851", {"start": v(-15.25, 15.28) * mm, "end": v(-19.25, 15.28) * mm, "construction": true});
            skLineSegment(sketch, "E852", {"start": v(-16.22, -31.94) * mm, "end": v(0, -31.94) * mm, "construction": true});
            skLineSegment(sketch, "E853", {"start": v(0, -31.94) * mm, "end": v(16.22, -31.94) * mm, "construction": true});
            skLineSegment(sketch, "E854", {"start": v(-12.6, -42.84) * mm, "end": v(0, -42.84) * mm, "construction": true});
            skLineSegment(sketch, "E855", {"start": v(0, -42.84) * mm, "end": v(12.6, -42.84) * mm, "construction": true});
            skFitSpline(sketch, "E856", {"points": [v(-11, -44.57) * mm, v(0, -48.1) * mm], "startDerivative": vector(9.3, -7.23) * mm, "endDerivative": vector(12, -2.3) * mm});
            skFitSpline(sketch, "E857", {"points": [v(11, -44.57) * mm, v(0, -48.1) * mm], "startDerivative": vector(-9.3, -7.23) * mm, "endDerivative": vector(-12, -2.3) * mm});
            skLineSegment(sketch, "E858", {"start": v(-7.9, -46.98) * mm, "end": v(0, -46.98) * mm, "construction": true});
            skLineSegment(sketch, "E859", {"start": v(0, -46.98) * mm, "end": v(7.9, -46.98) * mm, "construction": true});
            skLineSegment(sketch, "E860", {"start": v(-4, -47.35) * mm, "end": v(0, -47.35) * mm, "construction": true});
            skLineSegment(sketch, "E861", {"start": v(0, -47.35) * mm, "end": v(4, -47.35) * mm, "construction": true});
            skCircle(sketch, "E862", {"center": v(-8.33, -41.13) * mm, "radius": 1.5 * mm});
            skCircle(sketch, "E863", {"center": v(8.33, -41.13) * mm, "radius": 1.5 * mm});
            skFitSpline(sketch, "E864", {"points": [v(-15, 33.77) * mm, v(-19.25, 15.28) * mm], "startDerivative": vector(-1.66, -47.23) * mm, "endDerivative": vector(-4.95, -22.5) * mm});
            skFitSpline(sketch, "E865", {"points": [v(15, 33.77) * mm, v(19.25, 15.28) * mm], "startDerivative": vector(1.66, -47.23) * mm, "endDerivative": vector(4.95, -22.5) * mm});
            skLineSegment(sketch, "E866", {"start": v(-19.25, 15.28) * mm, "end": v(-19.25, -15.22) * mm});
            skLineSegment(sketch, "E867", {"start": v(19.25, 15.28) * mm, "end": v(19.25, -15.22) * mm});
            skArc(sketch, "E868.filletArc", {"start": v(-13.08, 33.76) * mm, "mid": v(-14.46, 33.21) * mm, "end": v(-15.08, 31.86) * mm});
            skArc(sketch, "E869.filletArc", {"start": v(15.08, 31.86) * mm, "mid": v(14.46, 33.21) * mm, "end": v(13.08, 33.76) * mm});
            skLineSegment(sketch, "E870", {"start": v(15.55, 18.03) * mm, "end": v(0, 18.03) * mm, "construction": true});
            skLineSegment(sketch, "E871", {"start": v(0, 18.03) * mm, "end": v(-15.55, 18.03) * mm, "construction": true});
            skPoint(sketch, "E872.visualSharp", {"position": v(-17.54, -26.16) * mm});
            skPoint(sketch, "E873.visualSharp", {"position": v(17.54, -26.16) * mm});
            skFitSpline(sketch, "E874", {"points": [v(-19.25, -15.22) * mm, v(-17.54, -26.16) * mm, v(-12.6, -42.84) * mm, v(-11, -44.57) * mm], "startDerivative": vector(1.48, -36.7) * mm, "endDerivative": vector(10.67, -6.67) * mm});
            skFitSpline(sketch, "E875", {"points": [v(19.25, -15.22) * mm, v(17.54, -26.16) * mm, v(12.6, -42.84) * mm, v(11, -44.57) * mm], "startDerivative": vector(-1.5, -36.7) * mm, "endDerivative": vector(-10.67, -6.67) * mm});
            skLineSegment(sketch, "E876", {"start": v(-8.33, -41.13) * mm, "end": v(-13.33, -41.13) * mm, "construction": true});
            skLineSegment(sketch, "E877", {"start": v(-8.33, -41.13) * mm, "end": v(-8.33, -46.13) * mm, "construction": true});
            skLineSegment(sketch, "E878", {"start": v(8.33, -41.13) * mm, "end": v(13.33, -41.13) * mm, "construction": true});
            skLineSegment(sketch, "E879", {"start": v(8.33, -41.13) * mm, "end": v(8.33, -46.13) * mm, "construction": true});
            skLineSegment(sketch, "E880", {"start": v(-11.5, 33.76) * mm, "end": v(-11.5, 29.76) * mm, "construction": true});
            skLineSegment(sketch, "E881", {"start": v(-11.5, 29.76) * mm, "end": v(-15.2, 29.76) * mm, "construction": true});
            skLineSegment(sketch, "E882", {"start": v(11.5, 33.76) * mm, "end": v(11.5, 29.76) * mm, "construction": true});
            skLineSegment(sketch, "E883", {"start": v(11.5, 29.76) * mm, "end": v(15.2, 29.76) * mm, "construction": true});
            skCircle(sketch, "E884", {"center": v(-11.5, 29.76) * mm, "radius": 1.5 * mm});
            skCircle(sketch, "E885", {"center": v(11.5, 29.76) * mm, "radius": 1.5 * mm});
            skCircle(sketch, "E886", {"center": v(-15.25, 15.28) * mm, "radius": 1.5 * mm});
            skCircle(sketch, "E887", {"center": v(15.25, 15.28) * mm, "radius": 1.5 * mm});
            skCircle(sketch, "E888", {"center": v(15.25, -15.22) * mm, "radius": 1.5 * mm});
            skCircle(sketch, "E889", {"center": v(-15.25, -15.22) * mm, "radius": 1.5 * mm});
            skLineSegment(sketch, "E890.bottom", {"start": v(-13.67, 13.7) * mm, "end": v(13.68, 13.7) * mm, "construction": true});
            skLineSegment(sketch, "E890.top", {"start": v(-13.67, -13.65) * mm, "end": v(13.68, -13.65) * mm, "construction": true});
            skLineSegment(sketch, "E890.left", {"start": v(-13.68, 13.7) * mm, "end": v(-13.68, -13.65) * mm, "construction": true});
            skLineSegment(sketch, "E890.right", {"start": v(13.67, 13.7) * mm, "end": v(13.67, -13.65) * mm, "construction": true});
            skLineSegment(sketch, "E891.bottom", {"start": v(-4.75, 4.78) * mm, "end": v(4.75, 4.78) * mm, "construction": true});
            skLineSegment(sketch, "E891.top", {"start": v(-4.75, -4.72) * mm, "end": v(4.75, -4.72) * mm, "construction": true});
            skLineSegment(sketch, "E891.left", {"start": v(-4.75, 4.78) * mm, "end": v(-4.75, -4.72) * mm, "construction": true});
            skLineSegment(sketch, "E891.right", {"start": v(4.75, 4.78) * mm, "end": v(4.75, -4.72) * mm, "construction": true});
            skPoint(sketch, "E892", {"position": v(-4.75, 0.03) * mm});
            skPoint(sketch, "E893", {"position": v(0, 4.78) * mm});
            skPoint(sketch, "E894", {"position": v(4.75, 0.03) * mm});
            skPoint(sketch, "E895", {"position": v(0, -4.72) * mm});
            skLineSegment(sketch, "E896", {"start": v(-6.16, 1.44) * mm, "end": v(-11.97, 7.25) * mm});
            skLineSegment(sketch, "E897", {"start": v(-6.16, -1.39) * mm, "end": v(-11.97, -7.19) * mm});
            skLineSegment(sketch, "E898", {"start": v(-13.68, -6.48) * mm, "end": v(-13.68, 6.54) * mm});
            skLineSegment(sketch, "E899", {"start": v(6.16, -1.39) * mm, "end": v(11.97, -7.19) * mm});
            skLineSegment(sketch, "E900", {"start": v(6.16, 1.44) * mm, "end": v(11.97, 7.25) * mm});
            skLineSegment(sketch, "E901", {"start": v(13.67, 6.54) * mm, "end": v(13.67, -6.48) * mm});
            skArc(sketch, "E902.filletArc", {"start": v(-6.16, -1.39) * mm, "mid": v(-5.58, 0.03) * mm, "end": v(-6.16, 1.44) * mm});
            skPoint(sketch, "E903.visualSharp", {"position": v(-13.67, 8.95) * mm});
            skArc(sketch, "E903.filletArc", {"start": v(-11.97, 7.25) * mm, "mid": v(-13.06, 7.46) * mm, "end": v(-13.67, 6.54) * mm});
            skPoint(sketch, "E904.visualSharp", {"position": v(-13.67, -8.9) * mm});
            skArc(sketch, "E904.filletArc", {"start": v(-13.67, -6.48) * mm, "mid": v(-13.06, -7.4) * mm, "end": v(-11.97, -7.19) * mm});
            skArc(sketch, "E905.filletArc", {"start": v(6.16, 1.44) * mm, "mid": v(5.58, 0.03) * mm, "end": v(6.16, -1.39) * mm});
            skPoint(sketch, "E906.visualSharp", {"position": v(13.68, 8.95) * mm});
            skArc(sketch, "E906.filletArc", {"start": v(13.68, 6.54) * mm, "mid": v(13.06, 7.46) * mm, "end": v(11.97, 7.25) * mm});
            skPoint(sketch, "E907.visualSharp", {"position": v(13.68, -8.9) * mm});
            skArc(sketch, "E907.filletArc", {"start": v(11.97, -7.19) * mm, "mid": v(13.06, -7.4) * mm, "end": v(13.68, -6.48) * mm});
            skLineSegment(sketch, "E908", {"start": v(1.41, -6.14) * mm, "end": v(7.22, -11.94) * mm});
            skLineSegment(sketch, "E909", {"start": v(-1.41, -6.14) * mm, "end": v(-7.22, -11.94) * mm});
            skLineSegment(sketch, "E910", {"start": v(-6.51, -13.65) * mm, "end": v(6.51, -13.65) * mm});
            skArc(sketch, "E911.filletArc", {"start": v(1.41, -6.14) * mm, "mid": v(0, -5.55) * mm, "end": v(-1.41, -6.14) * mm});
            skPoint(sketch, "E912.visualSharp", {"position": v(8.92, -13.65) * mm});
            skArc(sketch, "E912.filletArc", {"start": v(6.51, -13.65) * mm, "mid": v(7.43, -13.03) * mm, "end": v(7.22, -11.94) * mm});
            skPoint(sketch, "E913.visualSharp", {"position": v(-8.93, -13.65) * mm});
            skArc(sketch, "E913.filletArc", {"start": v(-7.22, -11.94) * mm, "mid": v(-7.43, -13.03) * mm, "end": v(-6.51, -13.65) * mm});
            skLineSegment(sketch, "E914", {"start": v(0, -17.8) * mm, "end": v(13.36, -17.8) * mm, "construction": true});
            skPoint(sketch, "E915", {"position": v(0, -17.8) * mm});
            skLineSegment(sketch, "E916", {"start": v(0, -17.8) * mm, "end": v(-13.36, -17.8) * mm, "construction": true});
            skLineSegment(sketch, "E917", {"start": v(-8.92, -13.65) * mm, "end": v(-8.92, -17.8) * mm, "construction": true});
            skLineSegment(sketch, "E918", {"start": v(8.92, -13.65) * mm, "end": v(8.92, -17.8) * mm, "construction": true});
            skLineSegment(sketch, "E919", {"start": v(0, -17.8) * mm, "end": v(0, -26.72) * mm, "construction": true});
            skLineSegment(sketch, "E920", {"start": v(-7.22, -19.5) * mm, "end": v(-1.41, -25.3) * mm});
            skLineSegment(sketch, "E921", {"start": v(1.41, -25.3) * mm, "end": v(7.22, -19.5) * mm});
            skLineSegment(sketch, "E922", {"start": v(6.51, -17.8) * mm, "end": v(-6.51, -17.8) * mm});
            skPoint(sketch, "E923.visualSharp", {"position": v(-8.92, -17.8) * mm});
            skArc(sketch, "E923.filletArc", {"start": v(-6.51, -17.8) * mm, "mid": v(-7.43, -18.42) * mm, "end": v(-7.22, -19.5) * mm});
            skPoint(sketch, "E924.visualSharp", {"position": v(8.92, -17.8) * mm});
            skArc(sketch, "E924.filletArc", {"start": v(7.22, -19.5) * mm, "mid": v(7.43, -18.42) * mm, "end": v(6.51, -17.8) * mm});
            skPoint(sketch, "E925.visualSharp", {"position": v(0, -26.72) * mm});
            skArc(sketch, "E925.filletArc", {"start": v(-1.41, -25.3) * mm, "mid": v(0, -25.9) * mm, "end": v(1.41, -25.3) * mm});
            skLineSegment(sketch, "E926", {"start": v(0, -21.22) * mm, "end": v(-11.7, -21.22) * mm, "construction": true});
            skLineSegment(sketch, "E927", {"start": v(0, -21.22) * mm, "end": v(11.7, -21.22) * mm, "construction": true});
            skLineSegment(sketch, "E928", {"start": v(-10.43, -22.48) * mm, "end": v(-4.5, -28.4) * mm});
            skLineSegment(sketch, "E929", {"start": v(-3.92, -29.82) * mm, "end": v(-3.92, -33) * mm});
            skLineSegment(sketch, "E930", {"start": v(-11.27, -22.95) * mm, "end": v(-9.07, -31.94) * mm});
            skArc(sketch, "E931", {"start": v(-9.07, -31.94) * mm, "mid": v(-6.94, -34.19) * mm, "end": v(-3.92, -33.5) * mm, "construction": true});
            skLineSegment(sketch, "E932", {"start": v(-4.32, -33.8) * mm, "end": v(-4.4, -33.86) * mm});
            skPoint(sketch, "E933", {"position": v(-6.94, -34.19) * mm});
            skArc(sketch, "E934", {"start": v(-9.07, -31.94) * mm, "mid": v(-7.22, -34.09) * mm, "end": v(-4.4, -33.86) * mm});
            skPoint(sketch, "E935.visualSharp", {"position": v(-11.7, -21.22) * mm});
            skArc(sketch, "E935.filletArc", {"start": v(-10.43, -22.48) * mm, "mid": v(-11.03, -22.4) * mm, "end": v(-11.27, -22.95) * mm});
            skPoint(sketch, "E936.visualSharp", {"position": v(-3.92, -29) * mm});
            skArc(sketch, "E936.filletArc", {"start": v(-3.92, -29.82) * mm, "mid": v(-4.07, -29.06) * mm, "end": v(-4.5, -28.4) * mm});
            skPoint(sketch, "E937.visualSharp", {"position": v(-3.92, -33.5) * mm});
            skArc(sketch, "E937.filletArc", {"start": v(-4.32, -33.8) * mm, "mid": v(-4.03, -33.44) * mm, "end": v(-3.92, -33) * mm});
            skLineSegment(sketch, "E938", {"start": v(10.43, -22.48) * mm, "end": v(4.5, -28.4) * mm});
            skLineSegment(sketch, "E939", {"start": v(3.92, -29.82) * mm, "end": v(3.92, -33) * mm});
            skLineSegment(sketch, "E940", {"start": v(3.92, -31.94) * mm, "end": v(9.07, -31.94) * mm, "construction": true});
            skArc(sketch, "E941", {"start": v(3.92, -33.5) * mm, "mid": v(6.94, -34.19) * mm, "end": v(9.07, -31.94) * mm, "construction": true});
            skLineSegment(sketch, "E942", {"start": v(11.27, -22.95) * mm, "end": v(9.07, -31.94) * mm});
            skLineSegment(sketch, "E943", {"start": v(4.32, -33.8) * mm, "end": v(4.4, -33.86) * mm});
            skPoint(sketch, "E944", {"position": v(6.94, -34.19) * mm});
            skArc(sketch, "E945", {"start": v(4.4, -33.86) * mm, "mid": v(7.22, -34.09) * mm, "end": v(9.07, -31.94) * mm});
            skPoint(sketch, "E946.visualSharp", {"position": v(3.92, -29) * mm});
            skArc(sketch, "E946.filletArc", {"start": v(4.5, -28.4) * mm, "mid": v(4.07, -29.06) * mm, "end": v(3.92, -29.82) * mm});
            skPoint(sketch, "E947.visualSharp", {"position": v(3.92, -33.5) * mm});
            skArc(sketch, "E947.filletArc", {"start": v(3.92, -33) * mm, "mid": v(4.03, -33.44) * mm, "end": v(4.32, -33.8) * mm});
            skPoint(sketch, "E948.visualSharp", {"position": v(11.7, -21.22) * mm});
            skArc(sketch, "E948.filletArc", {"start": v(11.27, -22.95) * mm, "mid": v(11.03, -22.4) * mm, "end": v(10.43, -22.48) * mm});
            skLineSegment(sketch, "E949", {"start": v(-8.92, -13.65) * mm, "end": v(-8.92, 13.7) * mm, "construction": true});
            skLineSegment(sketch, "E950", {"start": v(8.92, -13.65) * mm, "end": v(8.92, 13.7) * mm, "construction": true});
            skLineSegment(sketch, "E951", {"start": v(-1.41, 6.2) * mm, "end": v(-7.22, 12) * mm});
            skLineSegment(sketch, "E952", {"start": v(1.41, 6.2) * mm, "end": v(7.22, 12) * mm});
            skLineSegment(sketch, "E953", {"start": v(6.51, 13.7) * mm, "end": v(-6.51, 13.7) * mm});
            skArc(sketch, "E954.filletArc", {"start": v(-1.41, 6.2) * mm, "mid": v(0, 5.6) * mm, "end": v(1.41, 6.2) * mm});
            skPoint(sketch, "E955.visualSharp", {"position": v(8.92, 13.7) * mm});
            skArc(sketch, "E955.filletArc", {"start": v(7.22, 12) * mm, "mid": v(7.43, 13.09) * mm, "end": v(6.51, 13.7) * mm});
            skPoint(sketch, "E956.visualSharp", {"position": v(-8.93, 13.7) * mm});
            skArc(sketch, "E956.filletArc", {"start": v(-6.51, 13.7) * mm, "mid": v(-7.43, 13.09) * mm, "end": v(-7.22, 12) * mm});
            skLineSegment(sketch, "E957", {"start": v(0, 32.03) * mm, "end": v(8.5, 32.03) * mm, "construction": true});
            skPoint(sketch, "E957.endSnap0", {"position": v(0, 32.03) * mm});
            skLineSegment(sketch, "E958", {"start": v(0, 32.03) * mm, "end": v(-8.5, 32.03) * mm, "construction": true});
            skFitSpline(sketch, "E959", {"points": [v(-8.5, 32.03) * mm, v(-8.5, 33.77) * mm], "startDerivative": vector(0, 1.74) * mm, "endDerivative": vector(0, 1.74) * mm});
            skFitSpline(sketch, "E960", {"points": [v(8.5, 32.03) * mm, v(8.5, 33.77) * mm], "startDerivative": vector(0, 1.74) * mm, "endDerivative": vector(0, 1.74) * mm});
            skLineSegment(sketch, "E961", {"start": v(-9.5, 33.77) * mm, "end": v(-13.08, 33.76) * mm});
            skFitSpline(sketch, "E962", {"points": [v(8.5, 33.77) * mm, v(13.08, 33.76) * mm], "startDerivative": vector(4.35, 0) * mm, "endDerivative": vector(4.35, 0) * mm});
            skArc(sketch, "E963.filletArc", {"start": v(9.5, 33.77) * mm, "mid": v(8.8, 33.48) * mm, "end": v(8.5, 32.77) * mm});
            skArc(sketch, "E964.filletArc", {"start": v(-8.5, 32.77) * mm, "mid": v(-8.8, 33.48) * mm, "end": v(-9.5, 33.77) * mm});
            skLineSegment(sketch, "E965", {"start": v(-8.5, 32.29) * mm, "end": v(-8.5, 26.6) * mm});
            skLineSegment(sketch, "E966", {"start": v(8.5, 32.29) * mm, "end": v(8.5, 26.6) * mm});
            skFitSpline(sketch, "E967", {"points": [v(-8.5, 24.54) * mm, v(0, 22.26) * mm, v(8.5, 24.54) * mm], "startDerivative": vector(17.46, -6.82) * mm, "endDerivative": vector(17.46, 6.82) * mm});
            skArc(sketch, "E968.filletArc", {"start": v(-8.5, 26.6) * mm, "mid": v(-7.97, 24.88) * mm, "end": v(-6.56, 23.78) * mm});
            skArc(sketch, "E969.filletArc", {"start": v(6.56, 23.78) * mm, "mid": v(7.97, 24.88) * mm, "end": v(8.5, 26.6) * mm});
            skSolve(sketch);
        }
        {
            var Q0;
            Q0=qSketchRegion(id+"F6",true);
            extrude(context, id + "F7", {"entities" : qUnion([Q0]), "depth" : 21.5 * mm, "hasSecondDirection" : true, "secondDirectionOppositeDirection" : false, "secondDirectionDepth" : 20 * mm});
        }
        {
            var Q0;
            Q0=qSketchRegion(id+"F5",true);
            extrude(context, id + "F8", {"entities" : qUnion([Q0]), "depth" : 10.5 * mm, "hasSecondDirection" : true, "secondDirectionOppositeDirection" : false, "secondDirectionDepth" : 9 * mm});
        }
    });
